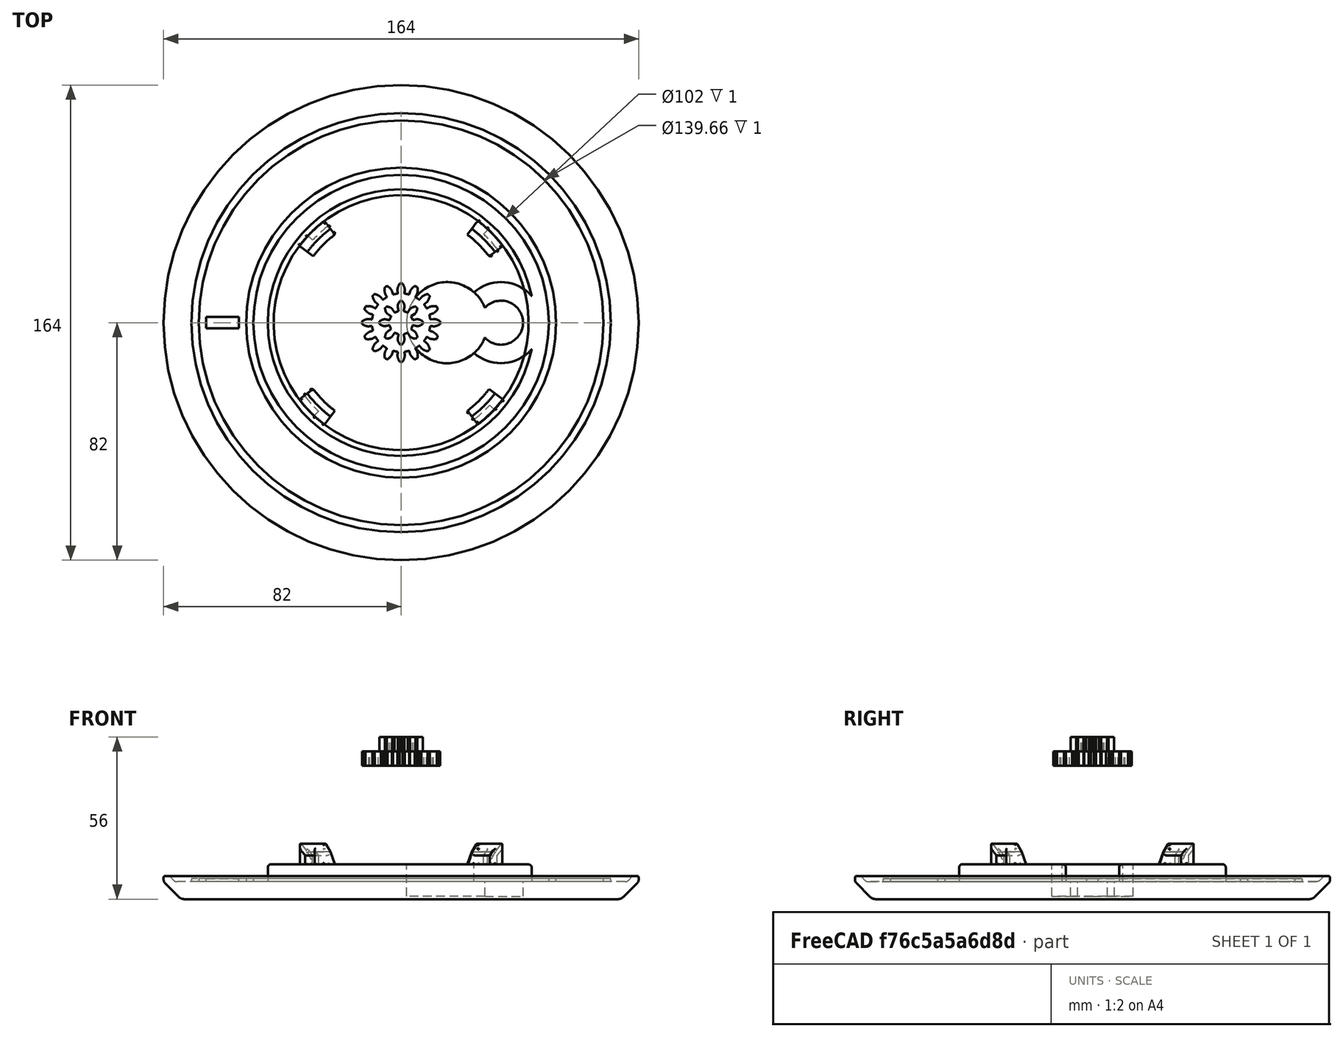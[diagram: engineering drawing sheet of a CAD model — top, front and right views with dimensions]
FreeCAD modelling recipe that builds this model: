
FCSTD DOCUMENT  (FreeCAD 1.0R39319 (Git))
Label: smart_medication_box_v2
License: All rights reserved
LicenseURL: https://en.wikipedia.org/wiki/All_rights_reserved
objects: Sketcher::SketchObject×25, PartDesign::Fillet×14, PartDesign::Body×11, PartDesign::Pad×8, PartDesign::Revolution×8, App::FeaturePython×7, PartDesign::Pocket×6, App::Link×6, PartDesign::PolarPattern×5, Part::FeaturePython×4, PartDesign::FeaturePython×3, TechDraw::DrawSVGTemplate×3, TechDraw::DrawProjGroupItem×3, TechDraw::DrawPage×3, PartDesign::Chamfer×2, TechDraw::DrawViewDimension×2, App::VarSet×1, PartDesign::AdditivePipe×1, Part::Cut×1, PartDesign::FeatureBase×1, +4 more types
note: 206 computed .brp shape members not serialized (recipe doc carries the construction recipe); baked Part::Feature solids carry a one-line shape summary decoded from their .brp

FEATURE [Part::FeaturePython] BevelGear  # WARN: FeaturePython — macro-defined, semantics opaque (R4)
  AttacherType = Attacher::AttachEngine3D
  angular_backlash = 0
  backlash = 0
  beta = 0
  clearance = 0.1
  dw = 32
  height = 7.5
  module = 2
  num_teeth = 16
  numpoints = 20
  pitch_angle = 45
  pressure_angle = 20
  reset_origin = true
  version = 1.3.0
  expr: angular_backlash = backlash / dw * 360 ° / pi
  expr: dw = num_teeth * module
  expr: height = 7.5
  expr: module = 2
  expr: num_teeth = 16
FEATURE [Sketcher::SketchObject] Sketch
  ArcFitTolerance = 1e-06
  AttachmentSupport = -> [Origin002]
  FullyConstrained = true
  MakeInternals = false
  MapMode = 5
  expr: Constraints[1] = 2 * VarSet.outer_ring_center_radius
  sketch-geometry (1):
    g0: Circle CenterX=0 CenterY=0 CenterZ=0 NormalX=0 NormalY=0 NormalZ=1 AngleXU=0 Radius=100
  constraints (2):
    c: Coincident(g0,g-1)
    c: Diameter(g0) = 200
FEATURE [App::VarSet] VarSet
  fillet_oouter_gear = 0.8
  outer_gear_section_length = 48
  outer_ring_bottom_width = 50
  outer_ring_center_radius = 100
  outer_ring_height = 36
  outer_ring_sides_angle = 30
  outer_wall_thickness = 2
  wall_thickness = 2
  expr: fillet_oouter_gear = 0.8
  expr: outer_ring_bottom_width = 50
  expr: outer_ring_center_radius = 100
  expr: outer_ring_height = 36
  expr: outer_ring_sides_angle = 30
FEATURE [Sketcher::SketchObject] Sketch002
  ArcFitTolerance = 1e-06
  FullyConstrained = true
  MakeInternals = false
  MapMode = 5
  Placement = pos=(100,0,0) rot=(1,0,0;1.5708rad)
  expr: Constraints[13] = VarSet.outer_ring_height
  expr: Constraints[16] = VarSet.outer_ring_sides_angle
  expr: Constraints[17] = VarSet.outer_ring_sides_angle
  expr: Constraints[19] = 5
  expr: Constraints[21] = VarSet.wall_thickness * 2
  expr: Constraints[24] = VarSet.wall_thickness
  expr: Constraints[28] = VarSet.outer_ring_bottom_width
  expr: Constraints[7] = VarSet.wall_thickness
  expr: Constraints[8] = VarSet.outer_ring_height
  expr: Constraints[9] = VarSet.wall_thickness
  sketch-geometry (10):
    g0: LineSegment StartX=26.1547 StartY=0 StartZ=0 EndX=46.9393 EndY=36 EndZ=0
    g1: LineSegment StartX=46.9393 StartY=36 StartZ=0 EndX=44.6299 EndY=36 EndZ=0
    g2: LineSegment StartX=44.6299 StartY=36 StartZ=0 EndX=25 EndY=2 EndZ=0
    g3: LineSegment StartX=25 StartY=2 StartZ=0 EndX=-25 EndY=2 EndZ=0
    g4: LineSegment StartX=-25 StartY=2 StartZ=0 EndX=-44.6299 EndY=36 EndZ=0
    g5: LineSegment StartX=-44.6299 StartY=36 StartZ=0 EndX=-49.2487 EndY=36 EndZ=0
    g6: LineSegment StartX=-26.1547 StartY=0 StartZ=0 EndX=26.1547 EndY=0 EndZ=0
    g7: LineSegment StartX=-49.2487 StartY=36 StartZ=0 EndX=-46.362 EndY=31 EndZ=0
    g8: LineSegment StartX=-44.0526 StartY=31 StartZ=0 EndX=-26.1547 EndY=0 EndZ=0
    g9: LineSegment StartX=-44.0526 StartY=31 StartZ=0 EndX=-46.362 EndY=31 EndZ=0
  constraints (29):
    c: Coincident(g1,g0)
    c: Coincident(g1,g2)
    c: Coincident(g2,g3)
    c: Coincident(g3,g4)
    c: Coincident(g4,g5)
    c: Horizontal(g5)
    c: Coincident(g6,g0)
    c: Distance(g0,g2) = 2
    c: DistanceY(g6,g4) = 36
    c: DistanceY(g6,g3) = 2
    c: Parallel(g3,g6)
    c: Parallel(g1,g-1)
    c: Parallel(g0,g2)
    c: Distance(g-1,g1) = 36
    c: Symmetric(g6,g0,g-2)
    c: PointOnObject(g0,g-1)
    c: Angle(g2,g-2) = 0.523599
    c: Angle(g-2,g4) = 0.523599
    c: Coincident(g7,g5)
    c: DistanceY(g7,g5) = 5
    c: Parallel(g7,g4)
    c: Distance(g4,g7) = 4
    c: Coincident(g8,g6)
    c: Parallel(g8,g4)
    c: Distance(g4,g8) = 2
    c: Coincident(g9,g8)
    c: Coincident(g9,g7)
    c: Parallel(g9,g5)
    c: DistanceX(g3,g3) = 50
FEATURE [PartDesign::AdditivePipe] AdditivePipe
  AuxilleryCurvelinear = true
  AuxillerySpineTangent = false
  Binormal = (0,0,0)
  Mode = 0
  Placement = pos=(100,0,0) rot=(1,0,0;1.5708rad)
  Profile = -> Sketch002
  Refine = true
  Spine = -> Sketch
  SpineTangent = false
  Suppressed = false
  Transformation = 0
  Transition = 0
FEATURE [PartDesign::Body] Body001  label="outer_sections_ring_gear"
  AllowCompound = false
  Group = -> [Sketch,Sketch002,AdditivePipe]
  Origin = -> Origin002
  Tip = -> AdditivePipe
FEATURE [PartDesign::FeaturePython] BevelGear001  # WARN: FeaturePython — macro-defined, semantics opaque (R4)
  AttacherType = Attacher::AttachEngine3D
  Suppressed = false
  angular_backlash = 0
  backlash = 0
  beta = 0
  clearance = 0.1
  dw = 96
  height = 5
  module = 1.5
  num_teeth = 64
  numpoints = 20
  pitch_angle = 30
  pressure_angle = 20
  reset_origin = true
  version = 1.3.0
  expr: angular_backlash = backlash / dw * 360 ° / pi
  expr: dw = num_teeth * module
  expr: module = 1.5
  expr: num_teeth = 64
  expr: pitch_angle = 30
FEATURE [PartDesign::Body] Body002  label="Body"
  AllowCompound = false
  Group = -> [BevelGear001]
  Origin = -> Origin004
  Placement = pos=(0,0,45) rot=(0,0,1;0rad)
  Tip = -> BevelGear001
FEATURE [Part::Cut] Cut
  Base = -> Body001
  Refine = true
  Tool = -> Body002
FEATURE [Sketcher::SketchObject] Sketch003
  ArcFitTolerance = 1e-06
  AttachmentSupport = -> [Origin006,XY_Plane003]
  FullyConstrained = true
  MakeInternals = true
  MapMode = 5
  expr: Constraints[0] = 104
  sketch-geometry (1):
    g0: Circle CenterX=0 CenterY=0 CenterZ=0 NormalX=0 NormalY=0 NormalZ=1 AngleXU=0 Radius=52
  constraints (2):
    c: Diameter(g0) = 104
    c: Coincident(g0,g-1)
FEATURE [PartDesign::Pad] Pad
  Direction = (0,0,1)
  Length = 6
  Length2 = 10
  Profile = -> Sketch003
  ReferenceAxis = -> Sketch003 [N_Axis]
  Refine = true
  Suppressed = false
  Type = 0
  expr: Length = 6
FEATURE [Sketcher::SketchObject] Sketch004
  ArcFitTolerance = 1e-06
  AttachmentSupport = -> [Pad]
  FullyConstrained = true
  MakeInternals = false
  MapMode = 5
  Placement = pos=(0,0,6) rot=(0,0,1;0rad)
  expr: Constraints[0] = 48 * 2 - 2
  sketch-geometry (1):
    g0: Circle CenterX=0 CenterY=0 CenterZ=0 NormalX=0 NormalY=0 NormalZ=1 AngleXU=0 Radius=47
  constraints (2):
    c: Diameter(g0) = 94
    c: Coincident(g0,g-1)
FEATURE [PartDesign::Pad] Pad001
  BaseFeature = -> Pad
  Direction = (0,0,1)
  Length = 6
  Length2 = 10
  Profile = -> Sketch004
  ReferenceAxis = -> Sketch004 [N_Axis]
  Refine = true
  Suppressed = false
  Type = 0
  expr: Length = 6
FEATURE [Part::FeaturePython] InvoluteGear  # WARN: FeaturePython — macro-defined, semantics opaque (R4)
  AttacherType = Attacher::AttachEngine3D
  Placement = pos=(0,0,41) rot=(0,0,1;0rad)
  addendum_diameter = 15
  angular_backlash = 0
  axle_hole = false
  axle_holesize = 10
  backlash = 0
  clearance = 0.25
  double_helix = false
  head = 0
  head_fillet = 0
  height = 5
  helix_angle = 0
  module = 1.5
  num_teeth = 8
  numpoints = 20
  offset_hole = false
  offset_holeoffset = 10
  offset_holesize = 10
  pitch_diameter = 12
  pressure_angle = 20
  properties_from_tool = false
  reversed_backlash = false
  root_diameter = 8.25
  root_fillet = 0
  shift = 0
  simple = false
  transverse_pitch = 4.71239
  traverse_module = 1.5
  undercut = false
  version = 1.3.0
  expr: angular_backlash = backlash / pitch_diameter * 360 ° / pi
  expr: module = 1.5
  expr: num_teeth = 8
FEATURE [Sketcher::SketchObject] Sketch005
  ArcFitTolerance = 1e-06
  AttachmentSupport = -> [Pad001]
  ExternalGeometry = -> [Pad001]
  FullyConstrained = true
  MakeInternals = false
  MapMode = 5
  Placement = pos=(0,0,12) rot=(0,0,1;0rad)
  expr: Constraints[0] = 28
  expr: Constraints[4] = 11.5
  sketch-geometry (2):
    g0: Circle CenterX=35.5 CenterY=0 CenterZ=0 NormalX=0 NormalY=0 NormalZ=1 AngleXU=0 Radius=14
    g1: Circle [constr] CenterX=35.5 CenterY=0 CenterZ=0 NormalX=0 NormalY=0 NormalZ=1 AngleXU=0 Radius=11.5
  constraints (5):
    c: Diameter(g0) = 28
    c: Coincident(g1,g0)
    c: Tangent(g1,g-3)
    c: PointOnObject(g0,g-1)
    c: Distance(g0,g-3) = 11.5
FEATURE [PartDesign::Pocket] Pocket001
  BaseFeature = -> Pad001
  Direction = (0,0,-1)
  Length = 6
  Length2 = 5
  Profile = -> Sketch005
  ReferenceAxis = -> Sketch005 [N_Axis]
  Refine = true
  Suppressed = false
  Type = 0
  expr: Length = 6
FEATURE [Sketcher::SketchObject] Sketch006
  ArcFitTolerance = 1e-06
  AttachmentSupport = -> [Pocket001]
  ExternalGeometry = -> [Pocket001]
  FullyConstrained = true
  MakeInternals = false
  MapMode = 5
  Placement = pos=(0,0,6) rot=(0,0,1;0rad)
  sketch-geometry (1):
    g0: Circle CenterX=35.5 CenterY=0 CenterZ=0 NormalX=0 NormalY=0 NormalZ=1 AngleXU=0 Radius=7.6
  constraints (2):
    c: Diameter(g0) = 15.2
    c: Coincident(g0,g-4)
FEATURE [PartDesign::Pocket] Pocket002
  BaseFeature = -> Pocket001
  Direction = (0,0,-1)
  Length = 5
  Length2 = 5
  Profile = -> Sketch006
  ReferenceAxis = -> Sketch006 [N_Axis]
  Refine = true
  Suppressed = false
  Type = 0
FEATURE [PartDesign::FeaturePython] InvoluteGear001  # WARN: FeaturePython — macro-defined, semantics opaque (R4)
  AttacherType = Attacher::AttachEngine3D
  Suppressed = false
  addendum_diameter = 27
  angular_backlash = 0
  axle_hole = false
  axle_holesize = 10
  backlash = 0
  clearance = 0.25
  double_helix = false
  head = 0
  head_fillet = 0
  height = 5
  helix_angle = 0
  module = 1.5
  num_teeth = 16
  numpoints = 20
  offset_hole = false
  offset_holeoffset = 10
  offset_holesize = 10
  pitch_diameter = 24
  pressure_angle = 20
  properties_from_tool = false
  reversed_backlash = false
  root_diameter = 20.25
  root_fillet = 0
  shift = 0
  simple = false
  transverse_pitch = 4.71239
  traverse_module = 1.5
  undercut = false
  version = 1.3.0
  expr: angular_backlash = backlash / pitch_diameter * 360 ° / pi
  expr: module = 1.5
  expr: num_teeth = 16
FEATURE [Sketcher::SketchObject] Sketch007
  ArcFitTolerance = 1e-06
  AttachmentSupport = -> [Pocket002]
  ExternalGeometry = -> [Pocket002]
  FullyConstrained = true
  MakeInternals = false
  MapMode = 5
  Placement = pos=(0,0,12) rot=(0,0,1;0rad)
  expr: Constraints[0] = 28
  expr: Constraints[2] = -3
  sketch-geometry (1):
    g0: Circle CenterX=16.9 CenterY=0 CenterZ=0 NormalX=0 NormalY=0 NormalZ=1 AngleXU=0 Radius=14
  constraints (3):
    c: Diameter(g0) = 28
    c: PointOnObject(g0,g-1)
    c: Distance(g0,g-3) = -3
FEATURE [PartDesign::Pocket] Pocket003
  BaseFeature = -> Pocket002
  Direction = (0,0,-1)
  Length = 11
  Length2 = 5
  Profile = -> Sketch007
  ReferenceAxis = -> Sketch007 [N_Axis]
  Refine = true
  Suppressed = false
  Type = 0
  expr: Length = 11
FEATURE [Sketcher::SketchObject] Sketch008
  ArcFitTolerance = 1e-06
  AttachmentSupport = -> [InvoluteGear001]
  FullyConstrained = true
  MakeInternals = false
  MapMode = 5
  Placement = pos=(0,0,5) rot=(0,0,1;0rad)
  expr: Constraints[11] = 3.1
  sketch-geometry (4):
    g0: ArcOfCircle CenterX=0 CenterY=0 CenterZ=0 NormalX=0 NormalY=0 NormalZ=1 AngleXU=0 Radius=2.5 StartAngle=2.47285 EndAngle=3.81034
    g1: ArcOfCircle CenterX=0 CenterY=0 CenterZ=0 NormalX=0 NormalY=0 NormalZ=1 AngleXU=0 Radius=2.5 StartAngle=5.61444 EndAngle=6.95193
    g2: LineSegment StartX=-1.9615 StartY=1.55 StartZ=0 EndX=1.9615 EndY=1.55 EndZ=0
    g3: LineSegment StartX=1.9615 StartY=-1.55 StartZ=0 EndX=-1.9615 EndY=-1.55 EndZ=0
  constraints (12):
    c: Coincident(g0,g-1)
    c: Coincident(g0,g1)
    c: Diameter(g0) = 5
    c: Equal(g1,g0)
    c: Coincident(g2,g0)
    c: Coincident(g2,g1)
    c: Coincident(g3,g1)
    c: Coincident(g3,g0)
    c: Parallel(g3,g2)
    c: Parallel(g-1,g2)
    c: Equal(g2,g3)
    c: Distance(g3,g2) = 3.1
FEATURE [PartDesign::Pocket] Pocket004
  BaseFeature = -> InvoluteGear001
  Direction = (0,0,-1)
  Length = 5
  Length2 = 5
  Profile = -> Sketch008
  ReferenceAxis = -> Sketch008 [N_Axis]
  Refine = true
  Suppressed = false
  Type = 0
FEATURE [App::Link] Body006  label="base"
  LinkedObject = -> Body003
FEATURE [Part::FeaturePython] InvoluteGear002  # WARN: FeaturePython — macro-defined, semantics opaque (R4)
  AttacherType = Attacher::AttachEngine3D
  Placement = pos=(0,0,46) rot=(0,0,1;0rad)
  addendum_diameter = 27
  angular_backlash = 0
  axle_hole = false
  axle_holesize = 10
  backlash = 0
  clearance = 0.25
  double_helix = false
  head = 0
  head_fillet = 0
  height = 5
  helix_angle = 0
  module = 1.5
  num_teeth = 16
  numpoints = 20
  offset_hole = false
  offset_holeoffset = 10
  offset_holesize = 10
  pitch_diameter = 24
  pressure_angle = 20
  properties_from_tool = false
  reversed_backlash = false
  root_diameter = 20.25
  root_fillet = 0
  shift = 0
  simple = false
  transverse_pitch = 4.71239
  traverse_module = 1.5
  undercut = false
  version = 1.3.0
  expr: angular_backlash = backlash / pitch_diameter * 360 ° / pi
  expr: module = 1.5
FEATURE [PartDesign::FeaturePython] InternalInvoluteGear  # WARN: FeaturePython — macro-defined, semantics opaque (R4)
  AttacherType = Attacher::AttachEngine3D
  Suppressed = false
  addendum_diameter = 94.2
  angular_backlash = 0
  backlash = 0
  clearance = 0.2
  double_helix = false
  head = -0.4
  head_fillet = 0
  height = 5
  helix_angle = 0
  module = 1.5
  num_teeth = 64
  numpoints = 20
  outside_diameter = 106
  pitch_diameter = 96
  pressure_angle = 20
  properties_from_tool = false
  reversed_backlash = false
  root_diameter = 99.6
  root_fillet = 0
  shift = 0
  simple = false
  thickness = 5
  transverse_pitch = 4.71239
  version = 1.3.0
  expr: angular_backlash = backlash / pitch_diameter * 360 ° / pi
  expr: clearance = 0.2
  expr: module = 1.5
  expr: num_teeth = 64
  expr: pressure_angle = 20
FEATURE [PartDesign::FeatureBase] BaseFeature002
  BaseFeature = -> InvoluteGear002
  Suppressed = false
FEATURE [PartDesign::Body] Body017
  AllowCompound = false
  BaseFeature = -> InvoluteGear002
  Group = -> [BaseFeature002]
  Origin = -> Origin028
  Placement = pos=(0,0,46) rot=(0,0,1;0rad)
  Tip = -> BaseFeature002
FEATURE [Part::FeaturePython] InvoluteGear003  # WARN: FeaturePython — macro-defined, semantics opaque (R4)
  AttacherType = Attacher::AttachEngine3D
  Placement = pos=(0,0,51) rot=(0,0,1;0rad)
  addendum_diameter = 15
  angular_backlash = 0
  axle_hole = false
  axle_holesize = 10
  backlash = 0
  clearance = 0.25
  double_helix = false
  head = 0
  head_fillet = 0
  height = 5
  helix_angle = 0
  module = 1.5
  num_teeth = 8
  numpoints = 20
  offset_hole = false
  offset_holeoffset = 10
  offset_holesize = 10
  pitch_diameter = 12
  pressure_angle = 20
  properties_from_tool = false
  reversed_backlash = false
  root_diameter = 8.25
  root_fillet = 0
  shift = 0
  simple = false
  transverse_pitch = 4.71239
  traverse_module = 1.5
  undercut = false
  version = 1.3.0
  expr: angular_backlash = backlash / pitch_diameter * 360 ° / pi
  expr: module = 1.5
  expr: num_teeth = 8
FEATURE [PartDesign::Boolean] Boolean
  Group = -> [InvoluteGear003,InvoluteGear002,Body017]
  Refine = true
  Suppressed = false
  Type = 0
  UsePlacement = true
FEATURE [App::Link] Body019  label="middle_gear"
  LinkPlacement = pos=(34.5001,-1.27229e-05,57) rot=(-0.64511,0.76409,0;3.14159rad)
  LinkedObject = -> Body018
  Placement = pos=(34.5001,-1.27229e-05,57) rot=(-0.64511,0.76409,0;3.14159rad)
FEATURE [App::Link] motor_gear001  label="motor_gear"
  LinkPlacement = pos=(15.9,0,1) rot=(0,0,-1;2.47285rad)
  LinkedObject = -> Body005
  Placement = pos=(15.9,0,1) rot=(0,0,-1;2.47285rad)
FEATURE [App::Link] outer_gear  label="pill_sections"
  LinkPlacement = pos=(7e-16,7e-16,6) rot=(0,0,1;0rad)
  LinkedObject = -> Body016
  Placement = pos=(7e-16,7e-16,6) rot=(0,0,1;0rad)
FEATURE [Sketcher::SketchObject] Sketch009
  ArcFitTolerance = 1e-06
  FullyConstrained = true
  MakeInternals = false
  MapMode = 5
  Placement = pos=(53,0,0) rot=(1,0,0;1.5708rad)
  expr: Constraints[10] = 2
  expr: Constraints[3] = 22
  sketch-geometry (17):
    g0: LineSegment StartX=0 StartY=0 StartZ=0 EndX=0 EndY=3 EndZ=0
    g1: LineSegment StartX=0 StartY=3 StartZ=0 EndX=21.1716 EndY=3 EndZ=0
    g2: LineSegment StartX=22.5858 StartY=3.58579 StartZ=0 EndX=23.7071 EndY=4.70711 EndZ=0
    g3: LineSegment StartX=24.4142 StartY=5 StartZ=0 EndX=25.4142 EndY=5 EndZ=0
    g4: LineSegment StartX=26.4142 StartY=4 StartZ=0 EndX=26.4142 EndY=3.82843 EndZ=0
    g5: LineSegment StartX=25.8284 StartY=2.41421 StartZ=0 EndX=24 EndY=0.585786 EndZ=0
    g6: LineSegment StartX=0 StartY=0 StartZ=0 EndX=22.5858 EndY=0 EndZ=0
    g7: ArcOfCircle CenterX=25.4142 CenterY=4 CenterZ=0 NormalX=0 NormalY=0 NormalZ=1 AngleXU=0 Radius=1 StartAngle=0 EndAngle=1.5708
    g8: GeomPoint [constr] X=26.4142 Y=5 Z=0
    g9: ArcOfCircle CenterX=24.4142 CenterY=4 CenterZ=0 NormalX=0 NormalY=0 NormalZ=1 AngleXU=0 Radius=1 StartAngle=1.5708 EndAngle=2.35619
    g10: GeomPoint [constr] X=24 Y=5 Z=0
    g11: ArcOfCircle CenterX=24.4142 CenterY=3.82843 CenterZ=0 NormalX=0 NormalY=0 NormalZ=1 AngleXU=0 Radius=2 StartAngle=5.49779 EndAngle=6.28319
    g12: GeomPoint [constr] X=26.4142 Y=3 Z=0
    g13: ArcOfCircle CenterX=21.1716 CenterY=5 CenterZ=0 NormalX=0 NormalY=0 NormalZ=1 AngleXU=0 Radius=2 StartAngle=4.71239 EndAngle=5.49779
    g14: GeomPoint [constr] X=22 Y=3 Z=0
    g15: ArcOfCircle CenterX=22.5858 CenterY=2 CenterZ=0 NormalX=0 NormalY=0 NormalZ=1 AngleXU=0 Radius=2 StartAngle=4.71239 EndAngle=5.49779
    g16: GeomPoint [constr] X=23.4142 Y=0 Z=0
  constraints (40):
    c: Coincident(g-1,g0)
    c: Coincident(g0,g1)
    c: PointOnObject(g0,g-2)
    c: DistanceX(g1,g14) = 22
    c: PointOnObject(g16,g-1)
    c: Coincident(g6,g0)
    c: Parallel(g1,g6)
    c: Parallel(g3,g1)
    c: Perpendicular(g3,g4)
    c: PointOnObject(g12,g1)
    c: DistanceY(g12,g8) = 2
    c: PointOnObject(g8,g3)
    c: PointOnObject(g8,g4)
    c: Tangent(g3,g7) = 1.5708
    c: Tangent(g4,g7) = 1.5708
    c: PointOnObject(g10,g2)
    c: PointOnObject(g10,g3)
    c: Tangent(g2,g9) = 1.5708
    c: Tangent(g3,g9) = 1.5708
    c: PointOnObject(g12,g5)
    c: PointOnObject(g12,g4)
    c: Tangent(g5,g11) = 1.5708
    c: Tangent(g4,g11) = 1.5708
    c: PointOnObject(g14,g2)
    c: PointOnObject(g14,g1)
    c: Tangent(g2,g13) = -1.5708
    c: Tangent(g1,g13) = -1.5708
    c: PointOnObject(g16,g5)
    c: PointOnObject(g16,g6)
    c: Tangent(g5,g15) = 1.5708
    c: Tangent(g6,g15) = -1.5708
    c: Equal(g9,g7)
    c: Equal(g13,g11)
    c: Equal(g11,g15)
    c: Radius(g9) = 1
    c: Radius(g13) = 2
    c: Parallel(g5,g2)
    c: Angle(g-1,g5) = 0.785398
    c: DistanceY(g0,g0) = 3
    c: Distance(g3,g3) = 1
FEATURE [PartDesign::Revolution] Revolution
  Angle = 360
  Angle2 = 60
  Axis = (1e-16,1e-16,1)
  Base = (0,0,0)
  BaseFeature = -> Pocket003
  Profile = -> Sketch009
  ReferenceAxis = -> Z_Axis003
  Refine = true
  Reversed = true
  Suppressed = false
  Type = 0
FEATURE [Sketcher::SketchObject] Sketch010
  ArcFitTolerance = 1e-06
  ExternalGeometry = -> [InternalInvoluteGear]
  FullyConstrained = false
  MakeInternals = false
  MapMode = 5
  Placement = pos=(53,0,0) rot=(1,0,0;1.5708rad)
  expr: Constraints[10] = VarSet.outer_wall_thickness
  expr: Constraints[11] = VarSet.outer_wall_thickness
  expr: Constraints[14] = VarSet.outer_wall_thickness
  expr: Constraints[17] = VarSet.fillet_oouter_gear
  expr: Constraints[2] = 5
  expr: Constraints[34] = VarSet.outer_wall_thickness
  expr: Constraints[36] = VarSet.outer_ring_height
  expr: Constraints[37] = VarSet.fillet_oouter_gear
  expr: Constraints[38] = 30
  expr: Constraints[45] = VarSet.fillet_oouter_gear
  expr: Constraints[50] = 25
  expr: Constraints[52] = 10
  expr: Constraints[6] = 25
  expr: Constraints[9] = VarSet.outer_wall_thickness
  sketch-geometry (28):
    g0: LineSegment StartX=0 StartY=0 StartZ=0 EndX=0 EndY=5 EndZ=0
    g1: LineSegment StartX=0 StartY=0 StartZ=0 EndX=24.0192 EndY=0 EndZ=0
    g2: LineSegment StartX=25.6005 StartY=0.775418 StartZ=0 EndX=40.7862 EndY=20.3842 EndZ=0
    g3: LineSegment StartX=24.6198 StartY=2.77542 StartZ=0 EndX=39.2049 EndY=21.6088 EndZ=0
    g4: LineSegment StartX=9.57963 StartY=2 StartZ=0 EndX=23.0385 EndY=2 EndZ=0
    g5: LineSegment StartX=0 StartY=5 StartZ=0 EndX=-2 EndY=5 EndZ=0
    g6: LineSegment StartX=-0.122418 StartY=35.2036 StartZ=0 EndX=4.22e-14 EndY=7.67973 EndZ=0
    g7: LineSegment StartX=8.57963 StartY=2.26795 StartZ=0 EndX=0.399992 EndY=6.99046 EndZ=0
    g8: ArcOfCircle CenterX=0.799992 CenterY=7.68328 CenterZ=0 NormalX=0 NormalY=0 NormalZ=1 AngleXU=0 Radius=0.8 StartAngle=3.14604 EndAngle=4.18879
    g9: ArcOfCircle CenterX=9.57963 CenterY=4 CenterZ=0 NormalX=0 NormalY=0 NormalZ=1 AngleXU=0 Radius=2 StartAngle=4.18879 EndAngle=4.71239
    g10: GeomPoint [constr] X=9.04373 Y=2 Z=0
    g11: ArcOfCircle CenterX=23.0385 CenterY=4 CenterZ=0 NormalX=0 NormalY=0 NormalZ=1 AngleXU=0 Radius=2 StartAngle=4.71239 EndAngle=5.62423
    g12: GeomPoint [constr] X=24.0192 Y=2 Z=0
    g13: ArcOfCircle CenterX=24.0192 CenterY=2 CenterZ=0 NormalX=0 NormalY=0 NormalZ=1 AngleXU=0 Radius=2 StartAngle=4.71239 EndAngle=5.62423
    g14: GeomPoint [constr] X=25 Y=0 Z=0
    g15: GeomPoint [constr] X=29 Y=5.16508 Z=0
    g16: GeomPoint [constr] X=27 Y=5.84896 Z=0
    g17: ArcOfCircle CenterX=-0.92241 CenterY=35.2 CenterZ=0 NormalX=0 NormalY=0 NormalZ=1 AngleXU=0 Radius=0.8 StartAngle=0.00444768 EndAngle=1.5708
    g18: LineSegment StartX=-10.9224 StartY=36 StartZ=0 EndX=-5.92241 EndY=36 EndZ=0
    g19: ArcOfCircle CenterX=19.4391 CenterY=36.916 CenterZ=0 NormalX=0 NormalY=0 NormalZ=1 AngleXU=0 Radius=27 StartAngle=5.62423 EndAngle=6.21764
    g20: ArcOfCircle CenterX=19.4391 CenterY=36.916 CenterZ=0 NormalX=0 NormalY=0 NormalZ=1 AngleXU=0 Radius=25 StartAngle=5.62423 EndAngle=6.21662
    g21: ArcOfCircle CenterX=45.1819 CenterY=35.2 CenterZ=0 NormalX=0 NormalY=0 NormalZ=1 AngleXU=0 Radius=0.8 StartAngle=1.5708 EndAngle=3.07503
    g22: LineSegment StartX=45.5828 StartY=36 StartZ=0 EndX=45.1819 EndY=36 EndZ=0
    g23: ArcOfCircle CenterX=45.5828 CenterY=35.2 CenterZ=0 NormalX=0 NormalY=0 NormalZ=1 AngleXU=0 Radius=0.8 StartAngle=6.21764 EndAngle=7.85398
    g24: ArcOfCircle CenterX=-10.9224 CenterY=35.2 CenterZ=0 NormalX=0 NormalY=0 NormalZ=1 AngleXU=0 Radius=0.8 StartAngle=1.5708 EndAngle=3.66964
    g25: LineSegment StartX=-11.6134 StartY=34.7969 StartZ=0 EndX=-2.05968 EndY=18.418 EndZ=0
    g26: LineSegment StartX=-2.05968 StartY=18.418 StartZ=0 EndX=-2 EndY=5 EndZ=0
    g27: LineSegment StartX=-5.92241 StartY=36 StartZ=0 EndX=-0.92241 EndY=36 EndZ=0
  constraints (66):
    c: Coincident(g0,g-1)
    c: PointOnObject(g0,g-2)
    c: DistanceY(g0,g0) = 5
    c: Coincident(g1,g0)
    c: PointOnObject(g14,g-1)
    c: Parallel(g3,g2)
    c: DistanceX(g1,g14) = 25
    c: DistanceX(g14,g15) = 4
    c: Parallel(g4,g1)
    c: Distance(g1,g4) = 2
    c: DistanceX(g16,g15) = 2
    c: Distance(g14,g3) = 2
    c: Coincident(g5,g0)
    c: Horizontal(g5)
    c: DistanceX(g5,g5) = 2
    c: Tangent(g8,g7) = 1.5708
    c: Tangent(g8,g6) = -1.5708
    c: Radius(g8) = 0.8
    c: PointOnObject(g6,g-2)
    c: PointOnObject(g10,g7)
    c: PointOnObject(g10,g4)
    c: Tangent(g7,g9) = 1.5708
    c: Tangent(g4,g9) = -1.5708
    c: PointOnObject(g12,g4)
    c: PointOnObject(g12,g3)
    c: Tangent(g4,g11) = -1.5708
    c: Tangent(g3,g11) = -1.5708
    c: PointOnObject(g14,g1)
    c: PointOnObject(g14,g2)
    c: Tangent(g1,g13) = -1.5708
    c: Tangent(g2,g13) = -1.5708
    c: PointOnObject(g15,g2)
    c: PointOnObject(g16,g3)
    c: Equal(g13,g11)
    c: Distance(g0,g8) = 2
    c: Tangent(g17,g6) = 1.5708
    c: Distance(g18,g-1) = 36
    c: Radius(g17) = 0.8
    c: Angle(g7,g1) = 0.523599
    c: Equal(g11,g9)
    c: Coincident(g20,g19)
    c: Tangent(g20,g3) = -1.5708
    c: Tangent(g19,g2) = -1.5708
    c: Tangent(g22,g21) = -1.5708
    c: Tangent(g21,g20) = 1.5708
    c: Radius(g21) = 0.8
    c: Tangent(g23,g22) = -1.5708
    c: Tangent(g23,g19) = -1.5708
    c: Equal(g23,g21)
    c: Parallel(g22,g-1)
    c: Radius(g20) = 25
    c: Radius(g11) = 2
    c: DistanceX(g18,g27) = 10
    c: Tangent(g24,g18) = 1.5708
    c: Equal(g24,g17)
    c: Coincident(g26,g25)
    c: Coincident(g26,g5)
    c: Parallel(g26,g6)
    c: Tangent(g25,g24) = -1.5708
    c: Perpendicular(g-2,g18)
    c: Perpendicular(g-2,g27)
    c: Coincident(g18,g27)
    c: Tangent(g27,g17) = 1.5708
    c: Equal(g27,g18)
    c: Angle(g26,g25) = 0.523599
    c: Vertical(g18,g-3)
FEATURE [PartDesign::Revolution] Revolution001
  Angle = 360
  Angle2 = 60
  Axis = (1e-16,1e-16,1)
  Base = (0,0,0)
  BaseFeature = -> InternalInvoluteGear
  Profile = -> Sketch010
  ReferenceAxis = -> Z_Axis013
  Refine = true
  Reversed = true
  Suppressed = false
  Type = 0
FEATURE [Sketcher::SketchObject] Sketch011
  ArcFitTolerance = 1e-06
  ExternalGeometry = -> [Revolution001]
  FullyConstrained = true
  MakeInternals = false
  MapMode = 5
  Placement = pos=(53,0,0) rot=(1,0,0;1.5708rad)
  sketch-geometry (2):
    g0: LineSegment StartX=-0.92241 StartY=36 StartZ=0 EndX=45.1819 EndY=36 EndZ=0
    g1: LineSegment StartX=9.57963 StartY=2 StartZ=0 EndX=23.0385 EndY=2 EndZ=0
  constraints (4):
    c: Coincident(g0,g-11)
    c: Coincident(g0,g-7)
    c: Tangent(g1,g-6) = -1.5708
    c: Coincident(g1,g-8)
FEATURE [PartDesign::Revolution] Revolution002
  Angle = 1
  Angle2 = 60
  Axis = (1e-16,1e-16,1)
  Base = (0,0,0)
  BaseFeature = -> Revolution001
  Midplane = true
  Profile = -> Sketch011
  ReferenceAxis = -> Z_Axis013
  Refine = true
  Suppressed = false
  Type = 0
  expr: Angle = 1
FEATURE [PartDesign::PolarPattern] PolarPattern
  Angle = 360
  Axis = -> Z_Axis013
  BaseFeature = -> Revolution002
  Mode = 0
  Occurrences = 32
  Offset = 120
  Originals = -> [Revolution002]
  Refine = true
  Suppressed = false
  TransformMode = 0
  expr: Occurrences = 32
FEATURE [PartDesign::Fillet] Fillet
  Base = -> Revolution [Edge30]
  BaseFeature = -> Revolution
  Radius = 1
  Refine = true
  SupportTransform = false
  Suppressed = false
  UseAllEdges = false
FEATURE [PartDesign::Fillet] Fillet001
  Base = -> Boolean [Face4]
  BaseFeature = -> Boolean
  Radius = 0.25
  Refine = true
  SupportTransform = false
  Suppressed = false
  UseAllEdges = false
  expr: Radius = 0.25
FEATURE [PartDesign::Fillet] Fillet002
  Base = -> Fillet001 [Face4,Face243]
  BaseFeature = -> Fillet001
  Radius = 0.2
  Refine = true
  SupportTransform = false
  Suppressed = false
  UseAllEdges = false
  expr: Radius = 0.2
FEATURE [PartDesign::Body] Body018
  AllowCompound = false
  Group = -> [Boolean,Fillet001,Fillet002]
  Origin = -> Origin030
  Tip = -> Fillet002
FEATURE [PartDesign::Body] Body020  label="upper_cover"
  AllowCompound = false
  Origin = -> Origin032
FEATURE [Sketcher::SketchObject] Sketch012
  ArcFitTolerance = 1e-06
  AttachmentSupport = -> [Origin034]
  FullyConstrained = true
  MakeInternals = false
  MapMode = 5
  expr: Constraints[2] = 80
  sketch-geometry (3):
    g0: Circle CenterX=0 CenterY=0 CenterZ=0 NormalX=0 NormalY=0 NormalZ=1 AngleXU=0 Radius=21
    g1: Circle CenterX=0 CenterY=0 CenterZ=0 NormalX=0 NormalY=0 NormalZ=1 AngleXU=0 Radius=40
    g2: Circle CenterX=0 CenterY=0 CenterZ=0 NormalX=0 NormalY=0 NormalZ=1 AngleXU=0 Radius=38.5
  constraints (6):
    c: Diameter(g0) = 42
    c: Coincident(g0,g-1)
    c: Diameter(g1) = 80
    c: Coincident(g1,g0)
    c: Coincident(g2,g0)
    c: Diameter(g2) = 77
FEATURE [App::Link] upper_cover_display
  LinkPlacement = pos=(-2.4e-15,-3.3e-15,39) rot=(0,0,-1;6.08242rad)
  LinkedObject = -> Body021
  Placement = pos=(-2.4e-15,-3.3e-15,39) rot=(0,0,-1;6.08242rad)
FEATURE [Sketcher::SketchObject] Sketch015
  ArcFitTolerance = 1e-06
  AttachmentSupport = -> [PolarPattern]
  ExternalGeometry = -> [PolarPattern]
  FullyConstrained = true
  MakeInternals = false
  MapMode = 5
  Placement = pos=(4e-15,4e-15,36) rot=(0,0,1;0rad)
  expr: Constraints[13] = 9
  sketch-geometry (5):
    g0: Circle [constr] CenterX=0 CenterY=0 CenterZ=0 NormalX=0 NormalY=0 NormalZ=1 AngleXU=0 Radius=52.0776
    g1: Circle CenterX=0 CenterY=0 CenterZ=0 NormalX=0 NormalY=0 NormalZ=1 AngleXU=0 Radius=42.5776
    g2: Circle CenterX=0 CenterY=0 CenterZ=0 NormalX=0 NormalY=0 NormalZ=1 AngleXU=0 Radius=51.5776
    g3: LineSegment [constr] StartX=-42.5776 StartY=0 StartZ=0 EndX=-42.0776 EndY=0 EndZ=0
    g4: LineSegment [constr] StartX=-52.0776 StartY=0 StartZ=0 EndX=-51.5776 EndY=0 EndZ=0
  constraints (14):
    c: Coincident(g0,g-3)
    c: PointOnObject(g-4,g0)
    c: Coincident(g1,g0)
    c: Coincident(g2,g0)
    c: PointOnObject(g3,g1)
    c: PointOnObject(g3,g-3)
    c: PointOnObject(g3,g-1)
    c: PointOnObject(g3,g-1)
    c: PointOnObject(g4,g0)
    c: PointOnObject(g4,g2)
    c: PointOnObject(g4,g-1)
    c: PointOnObject(g4,g-1)
    c: Equal(g4,g3)
    c: Distance(g2,g1) = 9
FEATURE [PartDesign::Pocket] Pocket005
  BaseFeature = -> PolarPattern
  Direction = (0,0,-1)
  Length = 3
  Length2 = 5
  Profile = -> Sketch015
  ReferenceAxis = -> Sketch015 [N_Axis]
  Refine = true
  Suppressed = false
  Type = 0
  expr: Length = 3
FEATURE [PartDesign::Fillet] Fillet003
  Base = -> Pocket005 [Edge312,Edge949]
  BaseFeature = -> Pocket005
  Radius = 1
  Refine = true
  SupportTransform = false
  Suppressed = false
  UseAllEdges = false
  expr: Radius = 1
FEATURE [Sketcher::SketchObject] Sketch016
  ArcFitTolerance = 1e-06
  AttachmentSupport = -> [Fillet003]
  ExternalGeometry = -> [Fillet003]
  FullyConstrained = false
  MakeInternals = false
  MapMode = 5
  Placement = pos=(0,0,33) rot=(0,0,1;0rad)
  sketch-geometry (8):
    g0: ArcOfCircle CenterX=4e-15 CenterY=4e-15 CenterZ=0 NormalX=0 NormalY=0 NormalZ=1 AngleXU=0 Radius=44.0776 StartAngle=1.01451 EndAngle=1.42895
    g1: ArcOfCircle CenterX=4e-15 CenterY=4e-15 CenterZ=0 NormalX=0 NormalY=0 NormalZ=1 AngleXU=0 Radius=50.0776 StartAngle=1.01451 EndAngle=1.42895
    g2: LineSegment StartX=6.23147 StartY=43.6349 StartZ=0 EndX=7.07972 EndY=49.5746 EndZ=0
    g3: LineSegment StartX=23.2744 StartY=37.4318 StartZ=0 EndX=26.4426 EndY=42.5271 EndZ=0
    g4: LineSegment [constr] StartX=23.2744 StartY=37.4318 StartZ=0 EndX=23.0104 EndY=37.0071 EndZ=0
    g5: LineSegment [constr] StartX=26.4426 StartY=42.5271 StartZ=0 EndX=26.7066 EndY=42.9517 EndZ=0
    g6: LineSegment [constr] StartX=4e-15 StartY=4e-15 StartZ=0 EndX=-40.9495 EndY=14.9044 EndZ=0
    g7: LineSegment [constr] StartX=4e-15 StartY=4e-15 StartZ=0 EndX=14.9044 EndY=40.9495 EndZ=0
  constraints (22):
    c: Coincident(g0,g-4)
    c: Coincident(g1,g0)
    c: Coincident(g2,g0)
    c: Coincident(g2,g1)
    c: Coincident(g3,g0)
    c: Coincident(g3,g1)
    c: Equal(g2,g3)
    c: Perpendicular(g0,g2)
    c: Coincident(g4,g0)
    c: PointOnObject(g4,g-4)
    c: Coincident(g5,g1)
    c: PointOnObject(g5,g-3)
    c: Parallel(g4,g3)
    c: Parallel(g3,g5)
    c: Equal(g5,g4)
    c: Distance(g3,g3) = 6
    c: Coincident(g6,g0)
    c: Angle(g6,g-1) = 0.349066
    c: PointOnObject(g6,g-4)
    c: Coincident(g7,g0)
    c: Perpendicular(g6,g7)
    c: Equal(g7,g6)
FEATURE [PartDesign::Pad] Pad004
  BaseFeature = -> Fillet003
  Direction = (0,0,1)
  Length = 1.5
  Length2 = 10
  Profile = -> Sketch016
  ReferenceAxis = -> Sketch016 [N_Axis]
  Refine = true
  Suppressed = false
  Type = 0
  expr: Length = 1.5
FEATURE [PartDesign::PolarPattern] PolarPattern002
  Angle = 360
  Axis = -> Sketch016 [N_Axis]
  BaseFeature = -> Pad004
  Mode = 0
  Occurrences = 2
  Offset = 120
  Originals = -> [Pad004]
  Refine = true
  Suppressed = false
  TransformMode = 0
FEATURE [PartDesign::Fillet] Fillet004
  Base = -> PolarPattern002 [Face177,Face175]
  BaseFeature = -> PolarPattern002
  Radius = 1
  Refine = true
  SupportTransform = false
  Suppressed = false
  UseAllEdges = false
FEATURE [PartDesign::Body] Body016  label="outer_gear"
  AllowCompound = false
  Group = -> [InternalInvoluteGear,Sketch010,Revolution001,Sketch011,Revolution002,PolarPattern,Sketch015,Pocket005,Fillet003,Sketch016,Pad004,PolarPattern002,Fillet004]
  Origin = -> Origin026
  Placement = pos=(0,0,41) rot=(0,0,1;0rad)
  Tip = -> Fillet004
FEATURE [PartDesign::Pad] Pad005
  Direction = (0,0,1)
  Length = 3
  Length2 = 10
  Profile = -> Sketch012 [Edge2,Edge1]
  ReferenceAxis = -> Sketch012 [N_Axis]
  Refine = true
  Suppressed = false
  Type = 0
  expr: Length = 3
FEATURE [Sketcher::SketchObject] Sketch017
  ArcFitTolerance = 1e-06
  FullyConstrained = true
  MakeInternals = false
  MapMode = 5
  Placement = pos=(40,0,0) rot=(1,0,0;1.5708rad)
  expr: Constraints[4] = 14
  sketch-geometry (6):
    g0: LineSegment StartX=5.78797 StartY=-27 StartZ=0 EndX=5.78797 EndY=-13 EndZ=0
    g1: LineSegment StartX=5.78797 StartY=-13 StartZ=0 EndX=0 EndY=0 EndZ=0
    g2: LineSegment StartX=0 StartY=0 StartZ=0 EndX=-1.5 EndY=0 EndZ=0
    g3: LineSegment StartX=-1.5 StartY=0 StartZ=0 EndX=4.28797 EndY=-13 EndZ=0
    g4: LineSegment StartX=4.28797 StartY=-13 StartZ=0 EndX=4.28797 EndY=-27 EndZ=0
    g5: LineSegment StartX=4.28797 StartY=-27 StartZ=0 EndX=5.78797 EndY=-27 EndZ=0
  constraints (17):
    c: Vertical(g0)
    c: Coincident(g1,g0)
    c: Coincident(g1,g-1)
    c: Angle(g0,g1) = 0.418879
    c: DistanceY(g0,g0) = 14
    c: DistanceY(g0,g1) = 27
    c: Coincident(g2,g1)
    c: PointOnObject(g2,g-1)
    c: Coincident(g2,g3)
    c: Coincident(g3,g4)
    c: Vertical(g4)
    c: Coincident(g4,g5)
    c: Coincident(g5,g0)
    c: Perpendicular(g4,g5)
    c: Equal(g3,g1)
    c: Parallel(g3,g1)
    c: DistanceX(g5,g5) = 1.5
FEATURE [PartDesign::Revolution] Revolution003
  Angle = 360
  Angle2 = 60
  Axis = (1e-16,1e-16,1)
  Base = (0,0,0)
  BaseFeature = -> Pad005
  Profile = -> Sketch017
  ReferenceAxis = -> Z_Axis017
  Refine = true
  Reversed = true
  Suppressed = false
  Type = 0
FEATURE [PartDesign::Chamfer] Chamfer
  Angle = 45
  Base = -> Revolution003 [Edge13,Edge10]
  BaseFeature = -> Revolution003
  ChamferType = 0
  FlipDirection = false
  Refine = true
  Size = 2
  Size2 = 1
  SupportTransform = false
  Suppressed = false
  UseAllEdges = false
FEATURE [Sketcher::SketchObject] Sketch018
  ArcFitTolerance = 1e-06
  FullyConstrained = true
  MakeInternals = false
  MapMode = 5
  Placement = pos=(44.288,-6.1e-15,-27) rot=(0,0.707107,0.707107;3.14159rad)
  sketch-geometry (4):
    g0: LineSegment StartX=0 StartY=0 StartZ=0 EndX=0 EndY=5.12132 EndZ=0
    g1: LineSegment StartX=0 StartY=5.12132 StartZ=0 EndX=2.12132 EndY=3 EndZ=0
    g2: LineSegment StartX=2.12132 StartY=3 StartZ=0 EndX=2.12132 EndY=0 EndZ=0
    g3: LineSegment StartX=2.12132 StartY=0 StartZ=0 EndX=0 EndY=0 EndZ=0
  constraints (11):
    c: Coincident(g-1,g0)
    c: Vertical(g0)
    c: Coincident(g0,g1)
    c: Coincident(g1,g2)
    c: PointOnObject(g2,g-1)
    c: Vertical(g2)
    c: Coincident(g2,g3)
    c: Coincident(g3,g0)
    c: Angle(g2,g1) = 0.785398
    c: Equal(g2,g1)
    c: DistanceY(g2,g2) = 3
FEATURE [PartDesign::Revolution] Revolution004
  Angle = 9
  Angle2 = 60
  Axis = (1e-16,1e-16,1)
  Base = (0,0,0)
  BaseFeature = -> Chamfer
  Profile = -> Sketch018
  ReferenceAxis = -> Z_Axis017
  Refine = true
  Suppressed = false
  Type = 0
  expr: Angle = 9
FEATURE [PartDesign::PolarPattern] PolarPattern003
  Angle = 360
  Axis = -> Z_Axis017
  BaseFeature = -> Revolution004
  Mode = 0
  Occurrences = 4
  Offset = 120
  Originals = -> [Revolution004]
  Refine = true
  Suppressed = false
  TransformMode = 0
FEATURE [Sketcher::SketchObject] Sketch019
  ArcFitTolerance = 1e-06
  AttachmentSupport = -> [Fillet]
  FullyConstrained = true
  MakeInternals = false
  MapMode = 5
  Placement = pos=(0,0,12) rot=(0,0,1;0rad)
  sketch-geometry (1):
    g0: Circle CenterX=0 CenterY=0 CenterZ=0 NormalX=0 NormalY=0 NormalZ=1 AngleXU=0 Radius=44
  constraints (2):
    c: Diameter(g0) = 88
    c: Coincident(g0,g-1)
FEATURE [Sketcher::SketchObject] Sketch020
  ArcFitTolerance = 1e-06
  FullyConstrained = true
  MakeInternals = false
  MapMode = 5
  Placement = pos=(44,0,12) rot=(1,0,0;1.5708rad)
  sketch-geometry (9):
    g0: LineSegment StartX=-2.19203 StartY=0 StartZ=0 EndX=-2.19203 EndY=3.1 EndZ=0
    g1: LineSegment StartX=-2.19203 StartY=3.1 StartZ=0 EndX=0 EndY=5.29203 EndZ=0
    g2: LineSegment StartX=0 StartY=5.29203 StartZ=0 EndX=0 EndY=7.79203 EndZ=0
    g3: LineSegment StartX=-5.9535 StartY=0 StartZ=0 EndX=-2.19203 EndY=0 EndZ=0
    g4: LineSegment StartX=0 StartY=7.79203 StartZ=0 EndX=-3.44203 EndY=4.35 EndZ=0
    g5: LineSegment StartX=-3.44203 StartY=4.35 StartZ=0 EndX=-5.9535 EndY=0 EndZ=0
    g6: LineSegment [constr] StartX=-3.44203 StartY=4.35 StartZ=0 EndX=-2.19203 EndY=3.1 EndZ=0
    g7: LineSegment StartX=-2.19203 StartY=0 StartZ=0 EndX=0 EndY=0 EndZ=0
    g8: LineSegment StartX=0 StartY=0 StartZ=0 EndX=0 EndY=5.29203 EndZ=0
  constraints (24):
    c: PointOnObject(g0,g-1)
    c: Vertical(g0)
    c: Coincident(g0,g1)
    c: PointOnObject(g1,g-2)
    c: Coincident(g1,g2)
    c: Coincident(g3,g0)
    c: PointOnObject(g3,g-1)
    c: PointOnObject(g2,g-2)
    c: Angle(g1,g0) = 0.785398
    c: DistanceY(g0,g0) = 3.1
    c: Equal(g1,g0)
    c: DistanceY(g2,g2) = 2.5
    c: Coincident(g2,g4)
    c: Coincident(g4,g5)
    c: Coincident(g3,g5)
    c: Angle(g3,g5) = 1.0472
    c: Parallel(g4,g1)
    c: Coincident(g6,g4)
    c: Coincident(g6,g0)
    c: Perpendicular(g4,g6)
    c: Coincident(g7,g0)
    c: Coincident(g7,g-1)
    c: Coincident(g8,g7)
    c: Coincident(g8,g1)
FEATURE [PartDesign::Revolution] Revolution005
  Angle = 323
  Angle2 = 47
  Axis = (1e-16,1e-16,1)
  Base = (0,0,0)
  BaseFeature = -> Fillet
  Profile = -> Sketch020 [Edge4,Edge5,Edge2,Edge1,Edge3,Edge6]
  ReferenceAxis = -> Z_Axis003
  Refine = true
  Reversed = true
  Suppressed = false
  Type = 4
  expr: Angle = 323
  expr: Angle2 = 47
FEATURE [PartDesign::Revolution] Revolution006
  Angle = 313
  Angle2 = 53
  Axis = (1e-16,1e-16,1)
  Base = (0,0,0)
  BaseFeature = -> Revolution005
  Profile = -> Sketch020 [Edge8,Edge3,Edge4,Edge5,Edge6,Edge7]
  ReferenceAxis = -> Z_Axis003
  Refine = true
  Reversed = true
  Suppressed = false
  Type = 4
  expr: Angle = 313
  expr: Angle2 = 53
FEATURE [PartDesign::PolarPattern] PolarPattern004
  Angle = 360
  Axis = -> Z_Axis003
  BaseFeature = -> Revolution006
  Mode = 0
  Occurrences = 4
  Offset = 120
  Originals = -> [Revolution005,Revolution006]
  Refine = true
  Suppressed = false
  TransformMode = 0
  expr: Occurrences = 4
FEATURE [PartDesign::Fillet] Fillet005
  Base = -> PolarPattern004 [Face5]
  BaseFeature = -> PolarPattern004
  Radius = 0.5
  Refine = true
  SupportTransform = false
  Suppressed = false
  UseAllEdges = false
  expr: Radius = 0.5
FEATURE [PartDesign::Fillet] Fillet006
  Base = -> Fillet005 [?Face21,Face20]
  BaseFeature = -> Fillet005
  Radius = 0.5
  Refine = true
  SupportTransform = false
  Suppressed = false
  UseAllEdges = false
  expr: Radius = 0.5
FEATURE [PartDesign::Fillet] Fillet007
  Base = -> Fillet006 [Face29,Face32]
  BaseFeature = -> Fillet006
  Radius = 0.5
  Refine = true
  SupportTransform = false
  Suppressed = false
  UseAllEdges = false
FEATURE [PartDesign::Fillet] Fillet008
  Base = -> Fillet007 [Face44,Face41]
  BaseFeature = -> Fillet007
  Radius = 0.5
  Refine = true
  SupportTransform = false
  Suppressed = false
  UseAllEdges = false
FEATURE [PartDesign::Fillet] Fillet009
  Base = -> PolarPattern003 [Face21,Face22,Face23,Face7]
  BaseFeature = -> PolarPattern003
  Radius = 0.5
  Refine = true
  SupportTransform = false
  Suppressed = false
  UseAllEdges = false
  expr: Radius = 0.5
FEATURE [PartDesign::Body] Body021  label="upper_cover_display"
  AllowCompound = false
  Group = -> [Sketch012,Pad005,Sketch017,Revolution003,Chamfer,Sketch018,Revolution004,PolarPattern003,Fillet009]
  Origin = -> Origin034
  Tip = -> Fillet009
FEATURE [Sketcher::SketchObject] Sketch021
  ArcFitTolerance = 1e-06
  AttachmentSupport = -> [Origin036]
  FullyConstrained = true
  MakeInternals = false
  MapMode = 5
  expr: Constraints[2] = 42.75 * 2
  expr: Constraints[3] = 51 * 2
  sketch-geometry (2):
    g0: Circle CenterX=0 CenterY=0 CenterZ=0 NormalX=0 NormalY=0 NormalZ=1 AngleXU=0 Radius=42.75
    g1: Circle CenterX=0 CenterY=0 CenterZ=0 NormalX=0 NormalY=0 NormalZ=1 AngleXU=0 Radius=51
  constraints (4):
    c: Coincident(g0,g-1)
    c: Coincident(g1,g0)
    c: Diameter(g0) = 85.5
    c: Diameter(g1) = 102
FEATURE [PartDesign::Pad] Pad006
  Direction = (0,0,1)
  Length = 3
  Length2 = 10
  Profile = -> Sketch021
  ReferenceAxis = -> Sketch021 [N_Axis]
  Refine = true
  Suppressed = false
  Type = 0
  expr: Length = 3
FEATURE [Sketcher::SketchObject] Sketch022
  ArcFitTolerance = 1e-06
  AttachmentSupport = -> [Pad006]
  FullyConstrained = false
  MakeInternals = false
  MapMode = 5
  Placement = pos=(0,0,3) rot=(0,0,1;0rad)
  sketch-geometry (4):
    g0: ArcOfCircle CenterX=0 CenterY=0 CenterZ=0 NormalX=0 NormalY=0 NormalZ=1 AngleXU=0 Radius=44.08 StartAngle=1.00282 EndAngle=1.41716
    g1: ArcOfCircle CenterX=0 CenterY=0 CenterZ=0 NormalX=0 NormalY=0 NormalZ=1 AngleXU=0 Radius=50.08 StartAngle=1.00282 EndAngle=1.41716
    g2: LineSegment StartX=6.74568 StartY=43.5608 StartZ=0 EndX=7.66388 EndY=49.4901 EndZ=0
    g3: LineSegment StartX=23.7119 StartY=37.159 StartZ=0 EndX=26.9394 EndY=42.217 EndZ=0
  constraints (11):
    c: Coincident(g1,g0)
    c: Coincident(g2,g0)
    c: Coincident(g2,g1)
    c: Coincident(g3,g0)
    c: Coincident(g3,g1)
    c: Equal(g2,g3)
    c: Perpendicular(g0,g2)
    c: Distance(g3,g3) = 6
    c: Radius(g0) = 44.08
    c: Angle(g0) = 0.414341
    c: Coincident(g0,g-1)
FEATURE [PartDesign::Pocket] Pocket006
  BaseFeature = -> Pad006
  Direction = (0,0,-1)
  Length = 1.5
  Length2 = 5
  Profile = -> Sketch022
  ReferenceAxis = -> Sketch022 [N_Axis]
  Refine = true
  Suppressed = false
  Type = 0
  expr: Length = 1.5
FEATURE [PartDesign::PolarPattern] PolarPattern005
  Angle = 360
  Axis = -> Sketch022 [N_Axis]
  BaseFeature = -> Pocket006
  Mode = 0
  Occurrences = 2
  Offset = 120
  Originals = -> [Pocket006]
  Refine = true
  Suppressed = false
  TransformMode = 0
FEATURE [PartDesign::Fillet] Fillet010
  Base = -> PolarPattern005 [Face2]
  BaseFeature = -> PolarPattern005
  Radius = 0.3
  Refine = true
  SupportTransform = false
  Suppressed = false
  UseAllEdges = false
  expr: Radius = 0.3
FEATURE [PartDesign::Fillet] Fillet011
  Base = -> Fillet010 [Face3]
  BaseFeature = -> Fillet010
  Radius = 0.4
  Refine = true
  SupportTransform = false
  Suppressed = false
  UseAllEdges = false
  expr: Radius = 0.4
FEATURE [Sketcher::SketchObject] Sketch023
  ArcFitTolerance = 1e-06
  AttachmentSupport = -> [Fillet011]
  FullyConstrained = false
  MakeInternals = false
  MapMode = 5
  Placement = pos=(0,0,0) rot=(1,0,0;3.14159rad)
  sketch-geometry (1190):
    g0: BSplineCurve PolesCount=2 KnotsCount=2 Degree=1 IsPeriodic=0
    g1: BSplineCurve PolesCount=2 KnotsCount=2 Degree=1 IsPeriodic=0
    g2: BSplineCurve PolesCount=2 KnotsCount=2 Degree=1 IsPeriodic=0
    g3: BSplineCurve PolesCount=2 KnotsCount=2 Degree=1 IsPeriodic=0
    g4: BSplineCurve PolesCount=2 KnotsCount=2 Degree=1 IsPeriodic=0
    g5: BSplineCurve PolesCount=2 KnotsCount=2 Degree=1 IsPeriodic=0
    g6: BSplineCurve PolesCount=2 KnotsCount=2 Degree=1 IsPeriodic=0
    g7: BSplineCurve PolesCount=2 KnotsCount=2 Degree=1 IsPeriodic=0
    g8: BSplineCurve PolesCount=2 KnotsCount=2 Degree=1 IsPeriodic=0
    g9: BSplineCurve PolesCount=2 KnotsCount=2 Degree=1 IsPeriodic=0
    g10: BSplineCurve PolesCount=2 KnotsCount=2 Degree=1 IsPeriodic=0
    g11: BSplineCurve PolesCount=2 KnotsCount=2 Degree=1 IsPeriodic=0
    g12: BSplineCurve PolesCount=2 KnotsCount=2 Degree=1 IsPeriodic=0
    g13: BSplineCurve PolesCount=2 KnotsCount=2 Degree=1 IsPeriodic=0
    g14: BSplineCurve PolesCount=2 KnotsCount=2 Degree=1 IsPeriodic=0
    g15: BSplineCurve PolesCount=2 KnotsCount=2 Degree=1 IsPeriodic=0
    g16: BSplineCurve PolesCount=2 KnotsCount=2 Degree=1 IsPeriodic=0
    g17: BSplineCurve PolesCount=2 KnotsCount=2 Degree=1 IsPeriodic=0
    g18: BSplineCurve PolesCount=2 KnotsCount=2 Degree=1 IsPeriodic=0
    g19: BSplineCurve PolesCount=2 KnotsCount=2 Degree=1 IsPeriodic=0
    g20: BSplineCurve PolesCount=2 KnotsCount=2 Degree=1 IsPeriodic=0
    g21: BSplineCurve PolesCount=2 KnotsCount=2 Degree=1 IsPeriodic=0
    g22: BSplineCurve PolesCount=2 KnotsCount=2 Degree=1 IsPeriodic=0
    g23: BSplineCurve PolesCount=2 KnotsCount=2 Degree=1 IsPeriodic=0
    g24: BSplineCurve PolesCount=2 KnotsCount=2 Degree=1 IsPeriodic=0
    g25: BSplineCurve PolesCount=2 KnotsCount=2 Degree=1 IsPeriodic=0
    g26: BSplineCurve PolesCount=2 KnotsCount=2 Degree=1 IsPeriodic=0
    g27: BSplineCurve PolesCount=2 KnotsCount=2 Degree=1 IsPeriodic=0
    g28: BSplineCurve PolesCount=2 KnotsCount=2 Degree=1 IsPeriodic=0
    g29: BSplineCurve PolesCount=2 KnotsCount=2 Degree=1 IsPeriodic=0
    g30: BSplineCurve PolesCount=2 KnotsCount=2 Degree=1 IsPeriodic=0
    g31: BSplineCurve PolesCount=2 KnotsCount=2 Degree=1 IsPeriodic=0
    g32: BSplineCurve PolesCount=2 KnotsCount=2 Degree=1 IsPeriodic=0
    g33: BSplineCurve PolesCount=2 KnotsCount=2 Degree=1 IsPeriodic=0
    g34: BSplineCurve PolesCount=2 KnotsCount=2 Degree=1 IsPeriodic=0
    g35: BSplineCurve PolesCount=2 KnotsCount=2 Degree=1 IsPeriodic=0
    g36: BSplineCurve PolesCount=2 KnotsCount=2 Degree=1 IsPeriodic=0
    g37: BSplineCurve PolesCount=2 KnotsCount=2 Degree=1 IsPeriodic=0
    g38: BSplineCurve PolesCount=2 KnotsCount=2 Degree=1 IsPeriodic=0
    g39: BSplineCurve PolesCount=2 KnotsCount=2 Degree=1 IsPeriodic=0
    g40: BSplineCurve PolesCount=2 KnotsCount=2 Degree=1 IsPeriodic=0
    g41: BSplineCurve PolesCount=2 KnotsCount=2 Degree=1 IsPeriodic=0
    g42: BSplineCurve PolesCount=2 KnotsCount=2 Degree=1 IsPeriodic=0
    g43: BSplineCurve PolesCount=2 KnotsCount=2 Degree=1 IsPeriodic=0
    g44: BSplineCurve PolesCount=2 KnotsCount=2 Degree=1 IsPeriodic=0
    g45: BSplineCurve PolesCount=2 KnotsCount=2 Degree=1 IsPeriodic=0
    g46: BSplineCurve PolesCount=2 KnotsCount=2 Degree=1 IsPeriodic=0
    g47: BSplineCurve PolesCount=2 KnotsCount=2 Degree=1 IsPeriodic=0
    g48: BSplineCurve PolesCount=2 KnotsCount=2 Degree=1 IsPeriodic=0
    g49: BSplineCurve PolesCount=2 KnotsCount=2 Degree=1 IsPeriodic=0
    g50: BSplineCurve PolesCount=2 KnotsCount=2 Degree=1 IsPeriodic=0
    g51: BSplineCurve PolesCount=2 KnotsCount=2 Degree=1 IsPeriodic=0
    g52: BSplineCurve PolesCount=2 KnotsCount=2 Degree=1 IsPeriodic=0
    g53: BSplineCurve PolesCount=2 KnotsCount=2 Degree=1 IsPeriodic=0
    g54: BSplineCurve PolesCount=2 KnotsCount=2 Degree=1 IsPeriodic=0
    g55: BSplineCurve PolesCount=2 KnotsCount=2 Degree=1 IsPeriodic=0
    g56: BSplineCurve PolesCount=2 KnotsCount=2 Degree=1 IsPeriodic=0
    g57: BSplineCurve PolesCount=2 KnotsCount=2 Degree=1 IsPeriodic=0
    g58: BSplineCurve PolesCount=2 KnotsCount=2 Degree=1 IsPeriodic=0
    g59: BSplineCurve PolesCount=2 KnotsCount=2 Degree=1 IsPeriodic=0
    g60: BSplineCurve PolesCount=2 KnotsCount=2 Degree=1 IsPeriodic=0
    g61: BSplineCurve PolesCount=2 KnotsCount=2 Degree=1 IsPeriodic=0
    g62: BSplineCurve PolesCount=2 KnotsCount=2 Degree=1 IsPeriodic=0
    g63: BSplineCurve PolesCount=2 KnotsCount=2 Degree=1 IsPeriodic=0
    g64: BSplineCurve PolesCount=2 KnotsCount=2 Degree=1 IsPeriodic=0
    g65: BSplineCurve PolesCount=2 KnotsCount=2 Degree=1 IsPeriodic=0
    g66: BSplineCurve PolesCount=2 KnotsCount=2 Degree=1 IsPeriodic=0
    g67: BSplineCurve PolesCount=2 KnotsCount=2 Degree=1 IsPeriodic=0
    g68: BSplineCurve PolesCount=2 KnotsCount=2 Degree=1 IsPeriodic=0
    g69: BSplineCurve PolesCount=2 KnotsCount=2 Degree=1 IsPeriodic=0
    g70: BSplineCurve PolesCount=2 KnotsCount=2 Degree=1 IsPeriodic=0
    g71: BSplineCurve PolesCount=2 KnotsCount=2 Degree=1 IsPeriodic=0
    g72: BSplineCurve PolesCount=2 KnotsCount=2 Degree=1 IsPeriodic=0
    g73: BSplineCurve PolesCount=2 KnotsCount=2 Degree=1 IsPeriodic=0
    g74: BSplineCurve PolesCount=2 KnotsCount=2 Degree=1 IsPeriodic=0
    g75: BSplineCurve PolesCount=2 KnotsCount=2 Degree=1 IsPeriodic=0
    g76: BSplineCurve PolesCount=2 KnotsCount=2 Degree=1 IsPeriodic=0
    g77: BSplineCurve PolesCount=2 KnotsCount=2 Degree=1 IsPeriodic=0
    g78: BSplineCurve PolesCount=2 KnotsCount=2 Degree=1 IsPeriodic=0
    g79: BSplineCurve PolesCount=2 KnotsCount=2 Degree=1 IsPeriodic=0
    g80: BSplineCurve PolesCount=2 KnotsCount=2 Degree=1 IsPeriodic=0
    g81: BSplineCurve PolesCount=2 KnotsCount=2 Degree=1 IsPeriodic=0
    g82: BSplineCurve PolesCount=2 KnotsCount=2 Degree=1 IsPeriodic=0
    g83: BSplineCurve PolesCount=2 KnotsCount=2 Degree=1 IsPeriodic=0
    g84: BSplineCurve PolesCount=2 KnotsCount=2 Degree=1 IsPeriodic=0
    g85: BSplineCurve PolesCount=2 KnotsCount=2 Degree=1 IsPeriodic=0
    g86: BSplineCurve PolesCount=2 KnotsCount=2 Degree=1 IsPeriodic=0
    g87: BSplineCurve PolesCount=2 KnotsCount=2 Degree=1 IsPeriodic=0
    g88: BSplineCurve PolesCount=2 KnotsCount=2 Degree=1 IsPeriodic=0
    g89: BSplineCurve PolesCount=2 KnotsCount=2 Degree=1 IsPeriodic=0
    g90: BSplineCurve PolesCount=2 KnotsCount=2 Degree=1 IsPeriodic=0
    g91: BSplineCurve PolesCount=2 KnotsCount=2 Degree=1 IsPeriodic=0
    g92: BSplineCurve PolesCount=2 KnotsCount=2 Degree=1 IsPeriodic=0
    g93: BSplineCurve PolesCount=2 KnotsCount=2 Degree=1 IsPeriodic=0
    g94: BSplineCurve PolesCount=2 KnotsCount=2 Degree=1 IsPeriodic=0
    g95: BSplineCurve PolesCount=2 KnotsCount=2 Degree=1 IsPeriodic=0
    g96: BSplineCurve PolesCount=2 KnotsCount=2 Degree=1 IsPeriodic=0
    g97: BSplineCurve PolesCount=2 KnotsCount=2 Degree=1 IsPeriodic=0
    g98: BSplineCurve PolesCount=2 KnotsCount=2 Degree=1 IsPeriodic=0
    g99: BSplineCurve PolesCount=2 KnotsCount=2 Degree=1 IsPeriodic=0
    g100: BSplineCurve PolesCount=2 KnotsCount=2 Degree=1 IsPeriodic=0
    g101: BSplineCurve PolesCount=2 KnotsCount=2 Degree=1 IsPeriodic=0
    g102: BSplineCurve PolesCount=2 KnotsCount=2 Degree=1 IsPeriodic=0
    g103: BSplineCurve PolesCount=2 KnotsCount=2 Degree=1 IsPeriodic=0
    g104: BSplineCurve PolesCount=2 KnotsCount=2 Degree=1 IsPeriodic=0
    g105: BSplineCurve PolesCount=2 KnotsCount=2 Degree=1 IsPeriodic=0
    g106: BSplineCurve PolesCount=2 KnotsCount=2 Degree=1 IsPeriodic=0
    g107: BSplineCurve PolesCount=2 KnotsCount=2 Degree=1 IsPeriodic=0
    g108: BSplineCurve PolesCount=2 KnotsCount=2 Degree=1 IsPeriodic=0
    g109: BSplineCurve PolesCount=2 KnotsCount=2 Degree=1 IsPeriodic=0
    g110: BSplineCurve PolesCount=2 KnotsCount=2 Degree=1 IsPeriodic=0
    g111: BSplineCurve PolesCount=2 KnotsCount=2 Degree=1 IsPeriodic=0
    g112: BSplineCurve PolesCount=2 KnotsCount=2 Degree=1 IsPeriodic=0
    g113: BSplineCurve PolesCount=2 KnotsCount=2 Degree=1 IsPeriodic=0
    g114: BSplineCurve PolesCount=2 KnotsCount=2 Degree=1 IsPeriodic=0
    g115: BSplineCurve PolesCount=2 KnotsCount=2 Degree=1 IsPeriodic=0
    g116: BSplineCurve PolesCount=2 KnotsCount=2 Degree=1 IsPeriodic=0
    g117: BSplineCurve PolesCount=2 KnotsCount=2 Degree=1 IsPeriodic=0
    g118: BSplineCurve PolesCount=2 KnotsCount=2 Degree=1 IsPeriodic=0
    g119: BSplineCurve PolesCount=2 KnotsCount=2 Degree=1 IsPeriodic=0
    g120: BSplineCurve PolesCount=2 KnotsCount=2 Degree=1 IsPeriodic=0
    g121: BSplineCurve PolesCount=2 KnotsCount=2 Degree=1 IsPeriodic=0
    g122: BSplineCurve PolesCount=2 KnotsCount=2 Degree=1 IsPeriodic=0
    g123: BSplineCurve PolesCount=2 KnotsCount=2 Degree=1 IsPeriodic=0
    g124: BSplineCurve PolesCount=2 KnotsCount=2 Degree=1 IsPeriodic=0
    g125: BSplineCurve PolesCount=2 KnotsCount=2 Degree=1 IsPeriodic=0
    g126: BSplineCurve PolesCount=2 KnotsCount=2 Degree=1 IsPeriodic=0
    g127: BSplineCurve PolesCount=2 KnotsCount=2 Degree=1 IsPeriodic=0
    g128: BSplineCurve PolesCount=3 KnotsCount=2 Degree=2 IsPeriodic=0
    g129: BSplineCurve PolesCount=3 KnotsCount=2 Degree=2 IsPeriodic=0
    g130: BSplineCurve PolesCount=3 KnotsCount=2 Degree=2 IsPeriodic=0
    g131: BSplineCurve PolesCount=3 KnotsCount=2 Degree=2 IsPeriodic=0
    g132: BSplineCurve PolesCount=3 KnotsCount=2 Degree=2 IsPeriodic=0
    g133: BSplineCurve PolesCount=3 KnotsCount=2 Degree=2 IsPeriodic=0
    g134: BSplineCurve PolesCount=3 KnotsCount=2 Degree=2 IsPeriodic=0
    g135: BSplineCurve PolesCount=3 KnotsCount=2 Degree=2 IsPeriodic=0
    g136: BSplineCurve PolesCount=3 KnotsCount=2 Degree=2 IsPeriodic=0
    g137: BSplineCurve PolesCount=3 KnotsCount=2 Degree=2 IsPeriodic=0
    g138: BSplineCurve PolesCount=3 KnotsCount=2 Degree=2 IsPeriodic=0
    g139: BSplineCurve PolesCount=3 KnotsCount=2 Degree=2 IsPeriodic=0
    g140: BSplineCurve PolesCount=3 KnotsCount=2 Degree=2 IsPeriodic=0
    g141: BSplineCurve PolesCount=3 KnotsCount=2 Degree=2 IsPeriodic=0
    g142: BSplineCurve PolesCount=3 KnotsCount=2 Degree=2 IsPeriodic=0
    g143: BSplineCurve PolesCount=3 KnotsCount=2 Degree=2 IsPeriodic=0
    g144: BSplineCurve PolesCount=2 KnotsCount=2 Degree=1 IsPeriodic=0
    g145: BSplineCurve PolesCount=2 KnotsCount=2 Degree=1 IsPeriodic=0
    g146: BSplineCurve PolesCount=2 KnotsCount=2 Degree=1 IsPeriodic=0
    g147: BSplineCurve PolesCount=2 KnotsCount=2 Degree=1 IsPeriodic=0
    g148: BSplineCurve PolesCount=2 KnotsCount=2 Degree=1 IsPeriodic=0
    g149: BSplineCurve PolesCount=2 KnotsCount=2 Degree=1 IsPeriodic=0
    g150: BSplineCurve PolesCount=2 KnotsCount=2 Degree=1 IsPeriodic=0
    g151: BSplineCurve PolesCount=2 KnotsCount=2 Degree=1 IsPeriodic=0
    g152: BSplineCurve PolesCount=2 KnotsCount=2 Degree=1 IsPeriodic=0
    g153: BSplineCurve PolesCount=2 KnotsCount=2 Degree=1 IsPeriodic=0
    g154: BSplineCurve PolesCount=2 KnotsCount=2 Degree=1 IsPeriodic=0
    g155: BSplineCurve PolesCount=2 KnotsCount=2 Degree=1 IsPeriodic=0
    g156: BSplineCurve PolesCount=3 KnotsCount=2 Degree=2 IsPeriodic=0
    g157: BSplineCurve PolesCount=3 KnotsCount=2 Degree=2 IsPeriodic=0
    g158: BSplineCurve PolesCount=3 KnotsCount=2 Degree=2 IsPeriodic=0
    g159: BSplineCurve PolesCount=3 KnotsCount=2 Degree=2 IsPeriodic=0
    g160: BSplineCurve PolesCount=3 KnotsCount=2 Degree=2 IsPeriodic=0
    g161: BSplineCurve PolesCount=3 KnotsCount=2 Degree=2 IsPeriodic=0
    g162: BSplineCurve PolesCount=3 KnotsCount=2 Degree=2 IsPeriodic=0
    g163: BSplineCurve PolesCount=3 KnotsCount=2 Degree=2 IsPeriodic=0
    g164: BSplineCurve PolesCount=3 KnotsCount=2 Degree=2 IsPeriodic=0
    g165: BSplineCurve PolesCount=3 KnotsCount=2 Degree=2 IsPeriodic=0
    g166: BSplineCurve PolesCount=2 KnotsCount=2 Degree=1 IsPeriodic=0
    g167: BSplineCurve PolesCount=3 KnotsCount=2 Degree=2 IsPeriodic=0
    g168: BSplineCurve PolesCount=3 KnotsCount=2 Degree=2 IsPeriodic=0
    g169: BSplineCurve PolesCount=3 KnotsCount=2 Degree=2 IsPeriodic=0
    g170: BSplineCurve PolesCount=3 KnotsCount=2 Degree=2 IsPeriodic=0
    g171: BSplineCurve PolesCount=3 KnotsCount=2 Degree=2 IsPeriodic=0
    g172: BSplineCurve PolesCount=3 KnotsCount=2 Degree=2 IsPeriodic=0
    g173: BSplineCurve PolesCount=3 KnotsCount=2 Degree=2 IsPeriodic=0
    g174: BSplineCurve PolesCount=3 KnotsCount=2 Degree=2 IsPeriodic=0
    g175: BSplineCurve PolesCount=3 KnotsCount=2 Degree=2 IsPeriodic=0
    g176: BSplineCurve PolesCount=2 KnotsCount=2 Degree=1 IsPeriodic=0
    g177: BSplineCurve PolesCount=2 KnotsCount=2 Degree=1 IsPeriodic=0
    g178: BSplineCurve PolesCount=2 KnotsCount=2 Degree=1 IsPeriodic=0
    g179: BSplineCurve PolesCount=3 KnotsCount=2 Degree=2 IsPeriodic=0
    g180: BSplineCurve PolesCount=3 KnotsCount=2 Degree=2 IsPeriodic=0
    g181: BSplineCurve PolesCount=3 KnotsCount=2 Degree=2 IsPeriodic=0
    g182: BSplineCurve PolesCount=3 KnotsCount=2 Degree=2 IsPeriodic=0
    g183: BSplineCurve PolesCount=2 KnotsCount=2 Degree=1 IsPeriodic=0
    g184: BSplineCurve PolesCount=3 KnotsCount=2 Degree=2 IsPeriodic=0
    g185: BSplineCurve PolesCount=3 KnotsCount=2 Degree=2 IsPeriodic=0
    g186: BSplineCurve PolesCount=3 KnotsCount=2 Degree=2 IsPeriodic=0
    g187: BSplineCurve PolesCount=3 KnotsCount=2 Degree=2 IsPeriodic=0
    g188: BSplineCurve PolesCount=3 KnotsCount=2 Degree=2 IsPeriodic=0
    g189: BSplineCurve PolesCount=2 KnotsCount=2 Degree=1 IsPeriodic=0
    g190: BSplineCurve PolesCount=2 KnotsCount=2 Degree=1 IsPeriodic=0
    g191: BSplineCurve PolesCount=2 KnotsCount=2 Degree=1 IsPeriodic=0
    g192: BSplineCurve PolesCount=3 KnotsCount=2 Degree=2 IsPeriodic=0
    g193: BSplineCurve PolesCount=3 KnotsCount=2 Degree=2 IsPeriodic=0
    g194: BSplineCurve PolesCount=3 KnotsCount=2 Degree=2 IsPeriodic=0
    g195: BSplineCurve PolesCount=3 KnotsCount=2 Degree=2 IsPeriodic=0
    g196: BSplineCurve PolesCount=3 KnotsCount=2 Degree=2 IsPeriodic=0
    g197: BSplineCurve PolesCount=3 KnotsCount=2 Degree=2 IsPeriodic=0
    g198: BSplineCurve PolesCount=2 KnotsCount=2 Degree=1 IsPeriodic=0
    g199: BSplineCurve PolesCount=3 KnotsCount=2 Degree=2 IsPeriodic=0
    g200: BSplineCurve PolesCount=3 KnotsCount=2 Degree=2 IsPeriodic=0
    g201: BSplineCurve PolesCount=3 KnotsCount=2 Degree=2 IsPeriodic=0
    g202: BSplineCurve PolesCount=3 KnotsCount=2 Degree=2 IsPeriodic=0
    g203: BSplineCurve PolesCount=3 KnotsCount=2 Degree=2 IsPeriodic=0
    g204: BSplineCurve PolesCount=3 KnotsCount=2 Degree=2 IsPeriodic=0
    g205: BSplineCurve PolesCount=2 KnotsCount=2 Degree=1 IsPeriodic=0
    g206: BSplineCurve PolesCount=3 KnotsCount=2 Degree=2 IsPeriodic=0
    g207: BSplineCurve PolesCount=3 KnotsCount=2 Degree=2 IsPeriodic=0
    g208: BSplineCurve PolesCount=2 KnotsCount=2 Degree=1 IsPeriodic=0
    g209: BSplineCurve PolesCount=2 KnotsCount=2 Degree=1 IsPeriodic=0
    g210: BSplineCurve PolesCount=2 KnotsCount=2 Degree=1 IsPeriodic=0
    g211: BSplineCurve PolesCount=2 KnotsCount=2 Degree=1 IsPeriodic=0
    g212: BSplineCurve PolesCount=2 KnotsCount=2 Degree=1 IsPeriodic=0
    g213: BSplineCurve PolesCount=2 KnotsCount=2 Degree=1 IsPeriodic=0
    g214: BSplineCurve PolesCount=2 KnotsCount=2 Degree=1 IsPeriodic=0
    g215: BSplineCurve PolesCount=2 KnotsCount=2 Degree=1 IsPeriodic=0
    g216: BSplineCurve PolesCount=2 KnotsCount=2 Degree=1 IsPeriodic=0
    g217: BSplineCurve PolesCount=2 KnotsCount=2 Degree=1 IsPeriodic=0
    g218: BSplineCurve PolesCount=2 KnotsCount=2 Degree=1 IsPeriodic=0
    g219: BSplineCurve PolesCount=2 KnotsCount=2 Degree=1 IsPeriodic=0
    g220: BSplineCurve PolesCount=2 KnotsCount=2 Degree=1 IsPeriodic=0
    g221: BSplineCurve PolesCount=2 KnotsCount=2 Degree=1 IsPeriodic=0
    g222: BSplineCurve PolesCount=2 KnotsCount=2 Degree=1 IsPeriodic=0
    g223: BSplineCurve PolesCount=2 KnotsCount=2 Degree=1 IsPeriodic=0
    g224: BSplineCurve PolesCount=3 KnotsCount=2 Degree=2 IsPeriodic=0
    g225: BSplineCurve PolesCount=3 KnotsCount=2 Degree=2 IsPeriodic=0
    g226: BSplineCurve PolesCount=3 KnotsCount=2 Degree=2 IsPeriodic=0
    g227: BSplineCurve PolesCount=3 KnotsCount=2 Degree=2 IsPeriodic=0
    g228: BSplineCurve PolesCount=3 KnotsCount=2 Degree=2 IsPeriodic=0
    g229: BSplineCurve PolesCount=3 KnotsCount=2 Degree=2 IsPeriodic=0
    g230: BSplineCurve PolesCount=2 KnotsCount=2 Degree=1 IsPeriodic=0
    g231: BSplineCurve PolesCount=3 KnotsCount=2 Degree=2 IsPeriodic=0
    g232: BSplineCurve PolesCount=3 KnotsCount=2 Degree=2 IsPeriodic=0
    g233: BSplineCurve PolesCount=3 KnotsCount=2 Degree=2 IsPeriodic=0
    g234: BSplineCurve PolesCount=3 KnotsCount=2 Degree=2 IsPeriodic=0
    g235: BSplineCurve PolesCount=3 KnotsCount=2 Degree=2 IsPeriodic=0
    g236: BSplineCurve PolesCount=3 KnotsCount=2 Degree=2 IsPeriodic=0
    g237: BSplineCurve PolesCount=3 KnotsCount=2 Degree=2 IsPeriodic=0
    g238: BSplineCurve PolesCount=2 KnotsCount=2 Degree=1 IsPeriodic=0
    g239: BSplineCurve PolesCount=2 KnotsCount=2 Degree=1 IsPeriodic=0
    g240: BSplineCurve PolesCount=2 KnotsCount=2 Degree=1 IsPeriodic=0
    g241: BSplineCurve PolesCount=2 KnotsCount=2 Degree=1 IsPeriodic=0
    g242: BSplineCurve PolesCount=2 KnotsCount=2 Degree=1 IsPeriodic=0
    g243: BSplineCurve PolesCount=2 KnotsCount=2 Degree=1 IsPeriodic=0
    g244: BSplineCurve PolesCount=3 KnotsCount=2 Degree=2 IsPeriodic=0
    g245: BSplineCurve PolesCount=3 KnotsCount=2 Degree=2 IsPeriodic=0
    g246: BSplineCurve PolesCount=3 KnotsCount=2 Degree=2 IsPeriodic=0
    g247: BSplineCurve PolesCount=3 KnotsCount=2 Degree=2 IsPeriodic=0
    g248: BSplineCurve PolesCount=3 KnotsCount=2 Degree=2 IsPeriodic=0
    g249: BSplineCurve PolesCount=3 KnotsCount=2 Degree=2 IsPeriodic=0
    g250: BSplineCurve PolesCount=3 KnotsCount=2 Degree=2 IsPeriodic=0
    g251: BSplineCurve PolesCount=3 KnotsCount=2 Degree=2 IsPeriodic=0
    g252: BSplineCurve PolesCount=3 KnotsCount=2 Degree=2 IsPeriodic=0
    g253: BSplineCurve PolesCount=3 KnotsCount=2 Degree=2 IsPeriodic=0
    g254: BSplineCurve PolesCount=3 KnotsCount=2 Degree=2 IsPeriodic=0
    g255: BSplineCurve PolesCount=3 KnotsCount=2 Degree=2 IsPeriodic=0
    g256: BSplineCurve PolesCount=3 KnotsCount=2 Degree=2 IsPeriodic=0
    g257: BSplineCurve PolesCount=3 KnotsCount=2 Degree=2 IsPeriodic=0
    g258: BSplineCurve PolesCount=3 KnotsCount=2 Degree=2 IsPeriodic=0
    g259: BSplineCurve PolesCount=3 KnotsCount=2 Degree=2 IsPeriodic=0
    g260: BSplineCurve PolesCount=3 KnotsCount=2 Degree=2 IsPeriodic=0
    g261: BSplineCurve PolesCount=2 KnotsCount=2 Degree=1 IsPeriodic=0
    g262: BSplineCurve PolesCount=3 KnotsCount=2 Degree=2 IsPeriodic=0
    g263: BSplineCurve PolesCount=3 KnotsCount=2 Degree=2 IsPeriodic=0
    g264: BSplineCurve PolesCount=3 KnotsCount=2 Degree=2 IsPeriodic=0
    g265: BSplineCurve PolesCount=3 KnotsCount=2 Degree=2 IsPeriodic=0
    g266: BSplineCurve PolesCount=3 KnotsCount=2 Degree=2 IsPeriodic=0
    g267: BSplineCurve PolesCount=3 KnotsCount=2 Degree=2 IsPeriodic=0
    g268: BSplineCurve PolesCount=3 KnotsCount=2 Degree=2 IsPeriodic=0
    g269: BSplineCurve PolesCount=3 KnotsCount=2 Degree=2 IsPeriodic=0
    g270: BSplineCurve PolesCount=3 KnotsCount=2 Degree=2 IsPeriodic=0
    g271: BSplineCurve PolesCount=3 KnotsCount=2 Degree=2 IsPeriodic=0
    g272: BSplineCurve PolesCount=3 KnotsCount=2 Degree=2 IsPeriodic=0
    g273: BSplineCurve PolesCount=2 KnotsCount=2 Degree=1 IsPeriodic=0
    g274: BSplineCurve PolesCount=3 KnotsCount=2 Degree=2 IsPeriodic=0
    g275: BSplineCurve PolesCount=3 KnotsCount=2 Degree=2 IsPeriodic=0
    g276: BSplineCurve PolesCount=2 KnotsCount=2 Degree=1 IsPeriodic=0
    g277: BSplineCurve PolesCount=2 KnotsCount=2 Degree=1 IsPeriodic=0
    g278: BSplineCurve PolesCount=2 KnotsCount=2 Degree=1 IsPeriodic=0
    g279: BSplineCurve PolesCount=2 KnotsCount=2 Degree=1 IsPeriodic=0
    g280: BSplineCurve PolesCount=3 KnotsCount=2 Degree=2 IsPeriodic=0
    g281: BSplineCurve PolesCount=3 KnotsCount=2 Degree=2 IsPeriodic=0
    g282: BSplineCurve PolesCount=3 KnotsCount=2 Degree=2 IsPeriodic=0
    g283: BSplineCurve PolesCount=3 KnotsCount=2 Degree=2 IsPeriodic=0
    g284: BSplineCurve PolesCount=3 KnotsCount=2 Degree=2 IsPeriodic=0
    g285: BSplineCurve PolesCount=2 KnotsCount=2 Degree=1 IsPeriodic=0
    g286: BSplineCurve PolesCount=3 KnotsCount=2 Degree=2 IsPeriodic=0
    g287: BSplineCurve PolesCount=3 KnotsCount=2 Degree=2 IsPeriodic=0
    g288: BSplineCurve PolesCount=3 KnotsCount=2 Degree=2 IsPeriodic=0
    g289: BSplineCurve PolesCount=3 KnotsCount=2 Degree=2 IsPeriodic=0
    g290: BSplineCurve PolesCount=3 KnotsCount=2 Degree=2 IsPeriodic=0
    g291: BSplineCurve PolesCount=3 KnotsCount=2 Degree=2 IsPeriodic=0
    g292: BSplineCurve PolesCount=2 KnotsCount=2 Degree=1 IsPeriodic=0
    g293: BSplineCurve PolesCount=3 KnotsCount=2 Degree=2 IsPeriodic=0
    g294: BSplineCurve PolesCount=3 KnotsCount=2 Degree=2 IsPeriodic=0
    g295: BSplineCurve PolesCount=3 KnotsCount=2 Degree=2 IsPeriodic=0
    g296: BSplineCurve PolesCount=3 KnotsCount=2 Degree=2 IsPeriodic=0
    g297: BSplineCurve PolesCount=3 KnotsCount=2 Degree=2 IsPeriodic=0
    g298: BSplineCurve PolesCount=3 KnotsCount=2 Degree=2 IsPeriodic=0
    g299: BSplineCurve PolesCount=3 KnotsCount=2 Degree=2 IsPeriodic=0
    g300: BSplineCurve PolesCount=3 KnotsCount=2 Degree=2 IsPeriodic=0
    g301: BSplineCurve PolesCount=3 KnotsCount=2 Degree=2 IsPeriodic=0
    g302: BSplineCurve PolesCount=3 KnotsCount=2 Degree=2 IsPeriodic=0
    g303: BSplineCurve PolesCount=3 KnotsCount=2 Degree=2 IsPeriodic=0
    g304: BSplineCurve PolesCount=3 KnotsCount=2 Degree=2 IsPeriodic=0
    g305: BSplineCurve PolesCount=3 KnotsCount=2 Degree=2 IsPeriodic=0
    g306: BSplineCurve PolesCount=3 KnotsCount=2 Degree=2 IsPeriodic=0
    g307: BSplineCurve PolesCount=3 KnotsCount=2 Degree=2 IsPeriodic=0
    g308: BSplineCurve PolesCount=3 KnotsCount=2 Degree=2 IsPeriodic=0
    g309: BSplineCurve PolesCount=3 KnotsCount=2 Degree=2 IsPeriodic=0
    g310: BSplineCurve PolesCount=3 KnotsCount=2 Degree=2 IsPeriodic=0
    g311: BSplineCurve PolesCount=3 KnotsCount=2 Degree=2 IsPeriodic=0
    g312: BSplineCurve PolesCount=3 KnotsCount=2 Degree=2 IsPeriodic=0
    g313: BSplineCurve PolesCount=3 KnotsCount=2 Degree=2 IsPeriodic=0
    g314: BSplineCurve PolesCount=3 KnotsCount=2 Degree=2 IsPeriodic=0
    g315: BSplineCurve PolesCount=3 KnotsCount=2 Degree=2 IsPeriodic=0
    g316: BSplineCurve PolesCount=3 KnotsCount=2 Degree=2 IsPeriodic=0
    g317: BSplineCurve PolesCount=3 KnotsCount=2 Degree=2 IsPeriodic=0
    g318: BSplineCurve PolesCount=3 KnotsCount=2 Degree=2 IsPeriodic=0
    g319: BSplineCurve PolesCount=3 KnotsCount=2 Degree=2 IsPeriodic=0
    g320: BSplineCurve PolesCount=2 KnotsCount=2 Degree=1 IsPeriodic=0
    g321: BSplineCurve PolesCount=3 KnotsCount=2 Degree=2 IsPeriodic=0
    g322: BSplineCurve PolesCount=3 KnotsCount=2 Degree=2 IsPeriodic=0
    g323: BSplineCurve PolesCount=3 KnotsCount=2 Degree=2 IsPeriodic=0
    g324: BSplineCurve PolesCount=3 KnotsCount=2 Degree=2 IsPeriodic=0
    g325: BSplineCurve PolesCount=3 KnotsCount=2 Degree=2 IsPeriodic=0
    g326: BSplineCurve PolesCount=3 KnotsCount=2 Degree=2 IsPeriodic=0
    g327: BSplineCurve PolesCount=3 KnotsCount=2 Degree=2 IsPeriodic=0
    g328: BSplineCurve PolesCount=3 KnotsCount=2 Degree=2 IsPeriodic=0
    g329: BSplineCurve PolesCount=3 KnotsCount=2 Degree=2 IsPeriodic=0
    g330: BSplineCurve PolesCount=3 KnotsCount=2 Degree=2 IsPeriodic=0
    g331: BSplineCurve PolesCount=3 KnotsCount=2 Degree=2 IsPeriodic=0
    g332: BSplineCurve PolesCount=3 KnotsCount=2 Degree=2 IsPeriodic=0
    g333: BSplineCurve PolesCount=3 KnotsCount=2 Degree=2 IsPeriodic=0
    g334: BSplineCurve PolesCount=3 KnotsCount=2 Degree=2 IsPeriodic=0
    g335: BSplineCurve PolesCount=3 KnotsCount=2 Degree=2 IsPeriodic=0
    g336: BSplineCurve PolesCount=3 KnotsCount=2 Degree=2 IsPeriodic=0
    g337: BSplineCurve PolesCount=2 KnotsCount=2 Degree=1 IsPeriodic=0
    g338: BSplineCurve PolesCount=2 KnotsCount=2 Degree=1 IsPeriodic=0
    g339: BSplineCurve PolesCount=2 KnotsCount=2 Degree=1 IsPeriodic=0
    g340: BSplineCurve PolesCount=2 KnotsCount=2 Degree=1 IsPeriodic=0
    g341: BSplineCurve PolesCount=2 KnotsCount=2 Degree=1 IsPeriodic=0
    g342: BSplineCurve PolesCount=2 KnotsCount=2 Degree=1 IsPeriodic=0
    g343: BSplineCurve PolesCount=2 KnotsCount=2 Degree=1 IsPeriodic=0
    g344: BSplineCurve PolesCount=2 KnotsCount=2 Degree=1 IsPeriodic=0
    g345: BSplineCurve PolesCount=2 KnotsCount=2 Degree=1 IsPeriodic=0
    g346: BSplineCurve PolesCount=2 KnotsCount=2 Degree=1 IsPeriodic=0
    g347: BSplineCurve PolesCount=2 KnotsCount=2 Degree=1 IsPeriodic=0
    g348: BSplineCurve PolesCount=3 KnotsCount=2 Degree=2 IsPeriodic=0
    g349: BSplineCurve PolesCount=3 KnotsCount=2 Degree=2 IsPeriodic=0
    g350: BSplineCurve PolesCount=3 KnotsCount=2 Degree=2 IsPeriodic=0
    g351: BSplineCurve PolesCount=3 KnotsCount=2 Degree=2 IsPeriodic=0
    g352: BSplineCurve PolesCount=3 KnotsCount=2 Degree=2 IsPeriodic=0
    g353: BSplineCurve PolesCount=3 KnotsCount=2 Degree=2 IsPeriodic=0
    g354: BSplineCurve PolesCount=3 KnotsCount=2 Degree=2 IsPeriodic=0
    g355: BSplineCurve PolesCount=3 KnotsCount=2 Degree=2 IsPeriodic=0
    g356: BSplineCurve PolesCount=3 KnotsCount=2 Degree=2 IsPeriodic=0
    g357: BSplineCurve PolesCount=3 KnotsCount=2 Degree=2 IsPeriodic=0
    g358: BSplineCurve PolesCount=3 KnotsCount=2 Degree=2 IsPeriodic=0
    g359: BSplineCurve PolesCount=3 KnotsCount=2 Degree=2 IsPeriodic=0
    g360: BSplineCurve PolesCount=3 KnotsCount=2 Degree=2 IsPeriodic=0
    g361: BSplineCurve PolesCount=3 KnotsCount=2 Degree=2 IsPeriodic=0
    g362: BSplineCurve PolesCount=3 KnotsCount=2 Degree=2 IsPeriodic=0
    g363: BSplineCurve PolesCount=3 KnotsCount=2 Degree=2 IsPeriodic=0
    g364: BSplineCurve PolesCount=2 KnotsCount=2 Degree=1 IsPeriodic=0
    g365: BSplineCurve PolesCount=2 KnotsCount=2 Degree=1 IsPeriodic=0
    g366: BSplineCurve PolesCount=2 KnotsCount=2 Degree=1 IsPeriodic=0
    g367: BSplineCurve PolesCount=2 KnotsCount=2 Degree=1 IsPeriodic=0
    g368: BSplineCurve PolesCount=2 KnotsCount=2 Degree=1 IsPeriodic=0
    g369: BSplineCurve PolesCount=2 KnotsCount=2 Degree=1 IsPeriodic=0
    g370: BSplineCurve PolesCount=2 KnotsCount=2 Degree=1 IsPeriodic=0
    g371: BSplineCurve PolesCount=2 KnotsCount=2 Degree=1 IsPeriodic=0
    g372: BSplineCurve PolesCount=2 KnotsCount=2 Degree=1 IsPeriodic=0
    g373: BSplineCurve PolesCount=2 KnotsCount=2 Degree=1 IsPeriodic=0
    g374: BSplineCurve PolesCount=2 KnotsCount=2 Degree=1 IsPeriodic=0
    g375: BSplineCurve PolesCount=2 KnotsCount=2 Degree=1 IsPeriodic=0
    g376: BSplineCurve PolesCount=2 KnotsCount=2 Degree=1 IsPeriodic=0
    g377: BSplineCurve PolesCount=2 KnotsCount=2 Degree=1 IsPeriodic=0
    g378: BSplineCurve PolesCount=2 KnotsCount=2 Degree=1 IsPeriodic=0
    g379: BSplineCurve PolesCount=2 KnotsCount=2 Degree=1 IsPeriodic=0
    g380: BSplineCurve PolesCount=2 KnotsCount=2 Degree=1 IsPeriodic=0
    g381: BSplineCurve PolesCount=2 KnotsCount=2 Degree=1 IsPeriodic=0
    g382: BSplineCurve PolesCount=2 KnotsCount=2 Degree=1 IsPeriodic=0
    g383: BSplineCurve PolesCount=2 KnotsCount=2 Degree=1 IsPeriodic=0
    g384: BSplineCurve PolesCount=2 KnotsCount=2 Degree=1 IsPeriodic=0
    g385: BSplineCurve PolesCount=2 KnotsCount=2 Degree=1 IsPeriodic=0
    g386: BSplineCurve PolesCount=2 KnotsCount=2 Degree=1 IsPeriodic=0
    g387: BSplineCurve PolesCount=2 KnotsCount=2 Degree=1 IsPeriodic=0
    g388: BSplineCurve PolesCount=2 KnotsCount=2 Degree=1 IsPeriodic=0
    g389: BSplineCurve PolesCount=2 KnotsCount=2 Degree=1 IsPeriodic=0
    g390: BSplineCurve PolesCount=2 KnotsCount=2 Degree=1 IsPeriodic=0
    g391: BSplineCurve PolesCount=2 KnotsCount=2 Degree=1 IsPeriodic=0
    g392: BSplineCurve PolesCount=2 KnotsCount=2 Degree=1 IsPeriodic=0
    g393: BSplineCurve PolesCount=2 KnotsCount=2 Degree=1 IsPeriodic=0
    g394: BSplineCurve PolesCount=2 KnotsCount=2 Degree=1 IsPeriodic=0
    g395: BSplineCurve PolesCount=2 KnotsCount=2 Degree=1 IsPeriodic=0
    g396: BSplineCurve PolesCount=2 KnotsCount=2 Degree=1 IsPeriodic=0
    g397: BSplineCurve PolesCount=2 KnotsCount=2 Degree=1 IsPeriodic=0
    g398: BSplineCurve PolesCount=3 KnotsCount=2 Degree=2 IsPeriodic=0
    g399: BSplineCurve PolesCount=3 KnotsCount=2 Degree=2 IsPeriodic=0
    ... +790 more geometry lines
  constraints (1190):
    c: Coincident(g93,g94)
    c: Coincident(g92,g93)
    c: Coincident(g282,g284)
    c: Coincident(g273,g274)
    c: Coincident(g272,g273)
    c: Coincident(g280,g282)
    c: Coincident(g88,g89)
    c: Coincident(g96,g97)
    c: Coincident(g299,g300)
    c: Coincident(g284,g286)
    c: Coincident(g298,g299)
    c: Coincident(g96,g99)
    c: Coincident(g89,g90)
    c: Coincident(g280,g281)
    c: Coincident(g271,g272)
    c: Coincident(g298,g304)
    c: Coincident(g300,g301)
    c: Coincident(g286,g288)
    c: Coincident(g274,g275)
    c: Coincident(g281,g283)
    c: Coincident(g303,g304)
    c: Coincident(g301,g302)
    c: Coincident(g288,g290)
    c: Coincident(g302,g303)
    c: Coincident(g283,g285)
    c: Coincident(g285,g287)
    c: Coincident(g290,g292)
    c: Coincident(g292,g294)
    c: Coincident(g270,g271)
    c: Coincident(g306,g308)
    c: Coincident(g287,g289)
    c: Coincident(g249,g251)
    c: Coincident(g314,g316)
    c: Coincident(g305,g306)
    c: Coincident(g308,g310)
    c: Coincident(g294,g296)
    c: Coincident(g251,g253)
    c: Coincident(g312,g314)
    c: Coincident(g263,g264)
    c: Coincident(g322,g324)
    c: Coincident(g316,g318)
    c: Coincident(g264,g265)
    c: Coincident(g289,g291)
    c: Coincident(g305,g307)
    c: Coincident(g324,g326)
    c: Coincident(g247,g249)
    c: Coincident(g310,g311)
    c: Coincident(g296,g297)
    c: Coincident(g262,g263)
    c: Coincident(g276,g277)
    c: Coincident(g320,g322)
    c: Coincident(g318,g320)
    c: Coincident(g265,g266)
    c: Coincident(g309,g311)
    c: Coincident(g275,g276)
    c: Coincident(g307,g309)
    c: Coincident(g291,g293)
    c: Coincident(g270,g279)
    c: Coincident(g325,g327)
    c: Coincident(g323,g325)
    c: Coincident(g100,g101)
    c: Coincident(g84,g85)
    c: Coincident(g253,g255)
    c: Coincident(g295,g297)
    c: Coincident(g277,g278)
    c: Coincident(g262,g269)
    c: Coincident(g312,g313)
    c: Coincident(g326,g327)
    c: Coincident(g247,g248)
    c: Coincident(g293,g295)
    c: Coincident(g329,g330)
    c: Coincident(g330,g331)
    c: Coincident(g278,g279)
    c: Coincident(g254,g256)
    c: Coincident(g266,g267)
    c: Coincident(g85,g86)
    c: Coincident(g100,g103)
    c: Coincident(g328,g329)
    c: Coincident(g321,g323)
    c: Coincident(g268,g269)
    c: Coincident(g267,g268)
    c: Coincident(g331,g332)
    c: Coincident(g94,g95)
    c: Coincident(g92,g95)
    c: Coincident(g252,g254)
    c: Coincident(g328,g336)
    c: Coincident(g248,g250)
    c: Coincident(g250,g252)
    c: Coincident(g332,g333)
    c: Coincident(g256,g258)
    c: Coincident(g319,g321)
    c: Coincident(g335,g336)
    c: Coincident(g255,g257)
    c: Coincident(g313,g315)
    c: Coincident(g88,g91)
    c: Coincident(g97,g98)
    c: Coincident(g260,g261)
    c: Coincident(g98,g99)
    c: Coincident(g90,g91)
    c: Coincident(g333,g334)
    c: Coincident(g259,g261)
    c: Coincident(g334,g335)
    c: Coincident(g258,g260)
    c: Coincident(g317,g319)
    c: Coincident(g348,g350)
    c: Coincident(g350,g352)
    c: Coincident(g315,g317)
    c: Coincident(g257,g259)
    c: Coincident(g357,g358)
    c: Coincident(g356,g357)
    c: Coincident(g228,g229)
    c: Coincident(g227,g228)
    c: Coincident(g346,g347)
    c: Coincident(g229,g230)
    c: Coincident(g352,g354)
    c: Coincident(g358,g359)
    c: Coincident(g231,g232)
    c: Coincident(g348,g349)
    c: Coincident(g230,g231)
    c: Coincident(g345,g346)
    c: Coincident(g356,g363)
    c: Coincident(g226,g227)
    c: Coincident(g232,g233)
    c: Coincident(g344,g345)
    c: Coincident(g238,g239)
    c: Coincident(g338,g339)
    c: Coincident(g237,g238)
    c: Coincident(g337,g347)
    c: Coincident(g359,g360)
    c: Coincident(g233,g234)
    c: Coincident(g236,g237)
    c: Coincident(g101,g102)
    c: Coincident(g84,g87)
    c: Coincident(g354,g355)
    c: Coincident(g243,g244)
    c: Coincident(g337,g338)
    c: Coincident(g362,g363)
    c: Coincident(g226,g246)
    c: Coincident(g349,g351)
    c: Coincident(g235,g236)
    c: Coincident(g234,g235)
    c: Coincident(g102,g103)
    c: Coincident(g86,g87)
    c: Coincident(g244,g245)
    c: Coincident(g80,g81)
    c: Coincident(g104,g105)
    c: Coincident(g245,g246)
    c: Coincident(g360,g361)
    c: Coincident(g361,g362)
    c: Coincident(g351,g353)
    c: Coincident(g242,g243)
    c: Coincident(g353,g355)
    c: Coincident(g239,g240)
    c: Coincident(g81,g82)
    c: Coincident(g104,g107)
    c: Coincident(g241,g242)
    c: Coincident(g340,g341)
    c: Coincident(g339,g340)
    c: Coincident(g240,g241)
    c: Coincident(g343,g344)
    c: Coincident(g341,g342)
    c: Coincident(g342,g343)
    c: Coincident(g384,g385)
    c: Coincident(g383,g384)
    c: Coincident(g382,g383)
    c: Coincident(g376,g377)
    c: Coincident(g214,g216)
    c: Coincident(g375,g385)
    c: Coincident(g373,g374)
    c: Coincident(g216,g218)
    c: Coincident(g80,g83)
    c: Coincident(g105,g106)
    c: Coincident(g375,g376)
    c: Coincident(g210,g212)
    c: Coincident(g220,g221)
    c: Coincident(g372,g373)
    c: Coincident(g221,g222)
    c: Coincident(g208,g210)
    c: Coincident(g222,g223)
    c: Coincident(g106,g107)
    c: Coincident(g82,g83)
    c: Coincident(g212,g214)
    c: Coincident(g371,g372)
    c: Coincident(g208,g209)
    c: Coincident(g219,g220)
    c: Coincident(g365,g366)
    c: Coincident(g213,g215)
    c: Coincident(g209,g211)
    c: Coincident(g364,g374)
    c: Coincident(g377,g378)
    c: Coincident(g211,g213)
    c: Coincident(g364,g365)
    c: Coincident(g381,g382)
    c: Coincident(g378,g379)
    c: Coincident(g380,g381)
    c: Coincident(g379,g380)
    c: Coincident(g223,g224)
    c: Coincident(g224,g225)
    c: Coincident(g219,g225)
    c: Coincident(g217,g218)
    c: Coincident(g108,g109)
    c: Coincident(g76,g77)
    c: Coincident(g215,g217)
    c: Coincident(g366,g367)
    c: Coincident(g370,g371)
    c: Coincident(g367,g368)
    c: Coincident(g369,g370)
    c: Coincident(g368,g369)
    c: Coincident(g108,g111)
    c: Coincident(g77,g78)
    c: Coincident(g419,g420)
    c: Coincident(g418,g419)
    c: Coincident(g109,g110)
    c: Coincident(g76,g79)
    c: Coincident(g78,g79)
    c: Coincident(g110,g111)
    c: Coincident(g181,g182)
    c: Coincident(g414,g415)
    c: Coincident(g413,g414)
    c: Coincident(g415,g416)
    c: Coincident(g182,g183)
    c: Coincident(g417,g418)
    c: Coincident(g412,g413)
    c: Coincident(g416,g417)
    c: Coincident(g397,g420)
    c: Coincident(g401,g402)
    c: Coincident(g402,g403)
    c: Coincident(g400,g401)
    c: Coincident(g180,g181)
    c: Coincident(g397,g398)
    c: Coincident(g183,g184)
    c: Coincident(g403,g404)
    c: Coincident(g399,g400)
    c: Coincident(g398,g399)
    c: Coincident(g395,g396)
    c: Coincident(g184,g185)
    c: Coincident(g411,g412)
    c: Coincident(g394,g395)
    c: Coincident(g404,g405)
    c: Coincident(g189,g190)
    c: Coincident(g185,g186)
    c: Coincident(g198,g199)
    c: Coincident(g179,g180)
    c: Coincident(g188,g189)
    c: Coincident(g405,g406)
    c: Coincident(g190,g191)
    c: Coincident(g407,g408)
    c: Coincident(g393,g394)
    c: Coincident(g197,g198)
    c: Coincident(g191,g192)
    c: Coincident(g410,g411)
    c: Coincident(g406,g407)
    c: Coincident(g186,g187)
    c: Coincident(g187,g188)
    c: Coincident(g205,g206)
    c: Coincident(g204,g205)
    c: Coincident(g387,g388)
    c: Coincident(g408,g409)
    c: Coincident(g199,g200)
    c: Coincident(g179,g207)
    c: Coincident(g196,g197)
    c: Coincident(g409,g410)
    c: Coincident(g192,g193)
    c: Coincident(g206,g207)
    c: Coincident(g386,g396)
    c: Coincident(g195,g196)
    c: Coincident(g203,g204)
    c: Coincident(g386,g387)
    c: Coincident(g193,g194)
    c: Coincident(g200,g201)
    c: Coincident(g194,g195)
    c: Coincident(g202,g203)
    c: Coincident(g201,g202)
    c: Coincident(g392,g393)
    c: Coincident(g388,g389)
    c: Coincident(g391,g392)
    c: Coincident(g389,g390)
    c: Coincident(g112,g113)
    c: Coincident(g72,g73)
    c: Coincident(g390,g391)
    c: Coincident(g73,g74)
    c: Coincident(g112,g115)
    c: Coincident(g72,g75)
    c: Coincident(g113,g114)
    c: Coincident(g432,g433)
    c: Coincident(g432,g460)
    c: Coincident(g74,g75)
    c: Coincident(g114,g115)
    c: Coincident(g438,g439)
    c: Coincident(g439,g440)
    c: Coincident(g459,g460)
    c: Coincident(g433,g434)
    c: Coincident(g437,g438)
    c: Coincident(g456,g457)
    c: Coincident(g440,g441)
    c: Coincident(g155,g178)
    c: Coincident(g455,g456)
    c: Coincident(g155,g156)
    c: Coincident(g458,g459)
    c: Coincident(g457,g458)
    c: Coincident(g445,g446)
    c: Coincident(g446,g447)
    c: Coincident(g434,g435)
    c: Coincident(g175,g176)
    c: Coincident(g454,g455)
    c: Coincident(g441,g442)
    c: Coincident(g156,g157)
    c: Coincident(g447,g448)
    c: Coincident(g444,g445)
    c: Coincident(g442,g443)
    c: Coincident(g436,g437)
    c: Coincident(g174,g175)
    c: Coincident(g443,g444)
    c: Coincident(g157,g158)
    c: Coincident(g430,g431)
    c: Coincident(g166,g167)
    c: Coincident(g435,g436)
    c: Coincident(g448,g449)
    c: Coincident(g429,g430)
    c: Coincident(g453,g454)
    c: Coincident(g173,g174)
    c: Coincident(g450,g451)
    c: Coincident(g449,g450)
    c: Coincident(g165,g166)
    c: Coincident(g158,g159)
    c: Coincident(g167,g168)
    c: Coincident(g164,g165)
    c: Coincident(g451,g452)
    c: Coincident(g452,g453)
    c: Coincident(g177,g178)
    c: Coincident(g159,g160)
    c: Coincident(g428,g429)
    c: Coincident(g176,g177)
    c: Coincident(g172,g173)
    c: Coincident(g163,g164)
    c: Coincident(g160,g161)
    c: Coincident(g422,g423)
    c: Coincident(g168,g169)
    c: Coincident(g161,g162)
    c: Coincident(g162,g163)
    c: Coincident(g171,g172)
    c: Coincident(g421,g431)
    c: Coincident(g170,g171)
    c: Coincident(g169,g170)
    c: Coincident(g421,g422)
    c: Coincident(g427,g428)
    c: Coincident(g423,g424)
    c: Coincident(g426,g427)
    c: Coincident(g424,g425)
    c: Coincident(g425,g426)
    c: Coincident(g68,g69)
    c: Coincident(g116,g117)
    c: Coincident(g116,g119)
    c: Coincident(g69,g70)
    c: Coincident(g68,g71)
    c: Coincident(g117,g118)
    c: Coincident(g118,g119)
    c: Coincident(g70,g71)
    c: Coincident(g473,g475)
    c: Coincident(g475,g477)
    c: Coincident(g472,g474)
    c: Coincident(g472,g473)
    c: Coincident(g477,g479)
    c: Coincident(g474,g476)
    c: Coincident(g476,g478)
    c: Coincident(g483,g484)
    c: Coincident(g479,g481)
    c: Coincident(g144,g154)
    c: Coincident(g144,g145)
    c: Coincident(g483,g489)
    c: Coincident(g488,g489)
    c: Coincident(g487,g488)
    c: Coincident(g481,g482)
    c: Coincident(g486,g487)
    c: Coincident(g485,g486)
    c: Coincident(g484,g485)
    c: Coincident(g147,g148)
    c: Coincident(g148,g149)
    c: Coincident(g145,g146)
    c: Coincident(g478,g480)
    c: Coincident(g480,g482)
    c: Coincident(g470,g471)
    c: Coincident(g469,g470)
    c: Coincident(g151,g152)
    c: Coincident(g146,g147)
    c: Coincident(g149,g150)
    c: Coincident(g153,g154)
    c: Coincident(g468,g469)
    c: Coincident(g152,g153)
    c: Coincident(g150,g151)
    c: Coincident(g462,g463)
    c: Coincident(g467,g468)
    c: Coincident(g461,g471)
    c: Coincident(g463,g464)
    c: Coincident(g461,g462)
    c: Coincident(g466,g467)
    c: Coincident(g464,g465)
    c: Coincident(g465,g466)
    c: Coincident(g64,g65)
    c: Coincident(g120,g121)
    c: Coincident(g121,g122)
    c: Coincident(g64,g67)
    c: Coincident(g120,g123)
    c: Coincident(g65,g66)
    c: Coincident(g122,g123)
    c: Coincident(g66,g67)
    c: Coincident(g501,g521)
    c: Coincident(g501,g502)
    c: Coincident(g520,g521)
    c: Coincident(g516,g517)
    c: Coincident(g515,g516)
    c: Coincident(g508,g509)
    c: Coincident(g507,g508)
    c: Coincident(g509,g510)
    c: Coincident(g502,g503)
    c: Coincident(g506,g507)
    c: Coincident(g519,g520)
    c: Coincident(g510,g511)
    c: Coincident(g134,g135)
    c: Coincident(g511,g512)
    c: Coincident(g132,g134)
    c: Coincident(g133,g135)
    c: Coincident(g139,g140)
    c: Coincident(g512,g513)
    c: Coincident(g505,g506)
    c: Coincident(g503,g504)
    c: Coincident(g518,g519)
    c: Coincident(g517,g518)
    c: Coincident(g138,g139)
    c: Coincident(g140,g141)
    c: Coincident(g513,g514)
    c: Coincident(g504,g505)
    c: Coincident(g514,g515)
    c: Coincident(g130,g132)
    c: Coincident(g137,g138)
    c: Coincident(g499,g500)
    c: Coincident(g498,g499)
    c: Coincident(g141,g142)
    c: Coincident(g131,g133)
    c: Coincident(g136,g137)
    c: Coincident(g142,g143)
    c: Coincident(g136,g143)
    c: Coincident(g128,g130)
    c: Coincident(g497,g498)
    c: Coincident(g129,g131)
    c: Coincident(g128,g129)
    c: Coincident(g496,g497)
    c: Coincident(g491,g492)
    c: Coincident(g492,g493)
    c: Coincident(g495,g496)
    c: Coincident(g490,g500)
    c: Coincident(g490,g491)
    c: Coincident(g493,g494)
    c: Coincident(g494,g495)
    c: Coincident(g124,g125)
    c: Coincident(g125,g126)
    c: Coincident(g60,g61)
    c: Coincident(g61,g62)
    c: Coincident(g60,g63)
    c: Coincident(g62,g63)
    c: Coincident(g124,g127)
    c: Coincident(g126,g127)
    c: Coincident(g1169,g1170)
    c: Coincident(g545,g547)
    c: Coincident(g1153,g1154)
    c: Coincident(g533,g534)
    c: Coincident(g1170,g1171)
    c: Coincident(g534,g536)
    c: Coincident(g1168,g1169)
    c: Coincident(g546,g547)
    c: Coincident(g533,g535)
    c: Coincident(g1152,g1153)
    c: Coincident(g548,g555)
    c: Coincident(g1154,g1155)
    c: Coincident(g1167,g1168)
    c: Coincident(g554,g555)
    c: Coincident(g548,g549)
    c: Coincident(g1161,g1162)
    c: Coincident(g1160,g1161)
    c: Coincident(g543,g545)
    c: Coincident(g544,g546)
    c: Coincident(g1171,g1172)
    c: Coincident(g536,g538)
    c: Coincident(g1166,g1167)
    c: Coincident(g1162,g1163)
    c: Coincident(g1159,g1160)
    c: Coincident(g553,g554)
    c: Coincident(g549,g550)
    c: Coincident(g535,g537)
    c: Coincident(g1155,g1156)
    c: Coincident(g1151,g1152)
    c: Coincident(g538,g540)
    c: Coincident(g1165,g1166)
    c: Coincident(g1175,g1176)
    c: Coincident(g1176,g1177)
    c: Coincident(g542,g544)
    c: Coincident(g1163,g1164)
    c: Coincident(g552,g553)
    c: Coincident(g1158,g1159)
    c: Coincident(g1164,g1165)
    c: Coincident(g550,g551)
    c: Coincident(g1172,g1173)
    c: Coincident(g1156,g1157)
    c: Coincident(g541,g543)
    c: Coincident(g540,g542)
    c: Coincident(g551,g552)
    c: Coincident(g1157,g1158)
    c: Coincident(g1174,g1175)
    c: Coincident(g537,g539)
    c: Coincident(g1177,g1178)
    c: Coincident(g1173,g1174)
    c: Coincident(g1150,g1151)
    c: Coincident(g539,g541)
    c: Coincident(g1150,g1178)
    c: Coincident(g1183,g1184)
    c: Coincident(g530,g531)
    c: Coincident(g1182,g1183)
    c: Coincident(g531,g532)
    c: Coincident(g1179,g1180)
    c: Coincident(g1179,g1189)
    c: Coincident(g528,g529)
    c: Coincident(g1184,g1185)
    c: Coincident(g1181,g1182)
    c: Coincident(g529,g530)
    c: Coincident(g527,g528)
    c: Coincident(g1180,g1181)
    c: Coincident(g524,g525)
    c: Coincident(g1185,g1186)
    c: Coincident(g523,g524)
    c: Coincident(g1186,g1187)
    c: Coincident(g526,g527)
    c: Coincident(g525,g526)
    c: Coincident(g522,g523)
    c: Coincident(g522,g532)
    c: Coincident(g1187,g1188)
    c: Coincident(g1188,g1189)
    c: Coincident(g56,g57)
    c: Coincident(g0,g1)
    c: Coincident(g0,g3)
    c: Coincident(g57,g58)
    c: Coincident(g1,g2)
    c: Coincident(g56,g59)
    c: Coincident(g2,g3)
    c: Coincident(g58,g59)
    c: Coincident(g575,g576)
    c: Coincident(g567,g576)
    c: Coincident(g1124,g1125)
    c: Coincident(g1125,g1126)
    c: Coincident(g572,g573)
    c: Coincident(g1123,g1124)
    c: Coincident(g1108,g1109)
    c: Coincident(g1122,g1123)
    c: Coincident(g1126,g1127)
    c: Coincident(g1109,g1110)
    c: Coincident(g1121,g1122)
    c: Coincident(g1116,g1117)
    c: Coincident(g567,g568)
    c: Coincident(g1107,g1108)
    c: Coincident(g1115,g1116)
    c: Coincident(g1117,g1118)
    c: Coincident(g1114,g1115)
    c: Coincident(g1120,g1121)
    c: Coincident(g568,g569)
    c: Coincident(g1118,g1119)
    c: Coincident(g571,g572)
    c: Coincident(g1127,g1128)
    c: Coincident(g1130,g1131)
    c: Coincident(g1131,g1132)
    c: Coincident(g1119,g1120)
    c: Coincident(g1110,g1111)
    c: Coincident(g1106,g1107)
    c: Coincident(g569,g570)
    c: Coincident(g1113,g1114)
    c: Coincident(g574,g575)
    c: Coincident(g573,g574)
    c: Coincident(g1129,g1130)
    c: Coincident(g1128,g1129)
    c: Coincident(g1111,g1112)
    c: Coincident(g1112,g1113)
    c: Coincident(g570,g571)
    c: Coincident(g1132,g1133)
    c: Coincident(g1105,g1106)
    c: Coincident(g1105,g1133)
    c: Coincident(g1139,g1141)
    c: Coincident(g1140,g1141)
    c: Coincident(g1146,g1147)
    c: Coincident(g562,g563)
    c: Coincident(g1145,g1146)
    c: Coincident(g564,g565)
    c: Coincident(g565,g566)
    c: Coincident(g1137,g1139)
    c: Coincident(g1138,g1140)
    c: Coincident(g561,g562)
    c: Coincident(g1147,g1148)
    c: Coincident(g558,g559)
    c: Coincident(g1144,g1145)
    c: Coincident(g563,g564)
    c: Coincident(g1148,g1149)
    c: Coincident(g1143,g1144)
    c: Coincident(g1135,g1137)
    c: Coincident(g1136,g1138)
    c: Coincident(g557,g558)
    c: Coincident(g560,g561)
    c: Coincident(g559,g560)
    c: Coincident(g1142,g1149)
    c: Coincident(g1142,g1143)
    c: Coincident(g1134,g1135)
    c: Coincident(g1134,g1136)
    c: Coincident(g556,g557)
    c: Coincident(g556,g566)
    c: Coincident(g4,g5)
    c: Coincident(g52,g53)
    c: Coincident(g5,g6)
    c: Coincident(g52,g55)
    c: Coincident(g53,g54)
    c: Coincident(g4,g7)
    c: Coincident(g54,g55)
    c: Coincident(g6,g7)
    c: Coincident(g599,g601)
    c: Coincident(g1068,g1069)
    c: Coincident(g1067,g1068)
    c: Coincident(g597,g599)
    c: Coincident(g1065,g1066)
    c: Coincident(g595,g597)
    c: Coincident(g1066,g1067)
    c: Coincident(g613,g615)
    c: Coincident(g601,g603)
    c: Coincident(g1069,g1070)
    c: Coincident(g589,g591)
    c: Coincident(g588,g589)
    c: Coincident(g615,g617)
    c: Coincident(g1064,g1065)
    c: Coincident(g613,g614)
    c: Coincident(g593,g595)
    c: Coincident(g591,g593)
    c: Coincident(g611,g612)
    c: Coincident(g1056,g1057)
    c: Coincident(g1057,g1058)
    c: Coincident(g606,g612)
    c: Coincident(g1056,g1079)
    c: Coincident(g617,g619)
    c: Coincident(g1063,g1064)
    c: Coincident(g1058,g1059)
    c: Coincident(g614,g616)
    c: Coincident(g588,g590)
    c: Coincident(g603,g605)
    c: Coincident(g1070,g1071)
    c: Coincident(g1059,g1060)
    c: Coincident(g610,g611)
    c: Coincident(g1076,g1077)
    c: Coincident(g1075,g1076)
    c: Coincident(g606,g607)
    c: Coincident(g618,g619)
    c: Coincident(g1062,g1063)
    c: Coincident(g1060,g1061)
    c: Coincident(g616,g618)
    c: Coincident(g1061,g1062)
    c: Coincident(g1074,g1075)
    c: Coincident(g600,g602)
    c: Coincident(g598,g600)
    c: Coincident(g604,g605)
    c: Coincident(g1071,g1072)
    c: Coincident(g609,g610)
    c: Coincident(g1073,g1074)
    c: Coincident(g602,g604)
    c: Coincident(g607,g608)
    c: Coincident(g1072,g1073)
    c: Coincident(g590,g592)
    c: Coincident(g596,g598)
    c: Coincident(g608,g609)
    c: Coincident(g1085,g1087)
    c: Coincident(g1087,g1089)
    c: Coincident(g583,g584)
    c: Coincident(g594,g596)
    c: Coincident(g1101,g1102)
    c: Coincident(g592,g594)
    c: Coincident(g1100,g1101)
    c: Coincident(g1083,g1085)
    c: Coincident(g1077,g1078)
    c: Coincident(g582,g583)
    c: Coincident(g1102,g1103)
    c: Coincident(g1089,g1091)
    c: Coincident(g1078,g1079)
    c: Coincident(g579,g580)
    c: Coincident(g1099,g1100)
    c: Coincident(g1086,g1088)
    c: Coincident(g585,g586)
    c: Coincident(g586,g587)
    c: Coincident(g1088,g1090)
    c: Coincident(g1103,g1104)
    c: Coincident(g1098,g1099)
    c: Coincident(g1084,g1086)
    c: Coincident(g1081,g1083)
    c: Coincident(g1091,g1093)
    c: Coincident(g581,g582)
    c: Coincident(g1097,g1098)
    c: Coincident(g584,g585)
    c: Coincident(g1096,g1104)
    c: Coincident(g580,g581)
    c: Coincident(g1096,g1097)
    c: Coincident(g1093,g1095)
    c: Coincident(g1090,g1092)
    c: Coincident(g1094,g1095)
    c: Coincident(g578,g579)
    c: Coincident(g1082,g1084)
    c: Coincident(g1092,g1094)
    c: Coincident(g1080,g1081)
    c: Coincident(g48,g49)
    c: Coincident(g8,g9)
    c: Coincident(g1080,g1082)
    c: Coincident(g577,g578)
    c: Coincident(g577,g587)
    c: Coincident(g9,g10)
    c: Coincident(g48,g51)
    c: Coincident(g8,g11)
    c: Coincident(g49,g50)
    c: Coincident(g1012,g1013)
    c: Coincident(g632,g634)
    c: Coincident(g50,g51)
    c: Coincident(g10,g11)
    c: Coincident(g1011,g1012)
    c: Coincident(g1009,g1010)
    c: Coincident(g1013,g1014)
    c: Coincident(g634,g636)
    c: Coincident(g654,g655)
    c: Coincident(g1010,g1011)
    c: Coincident(g631,g632)
    c: Coincident(g1008,g1009)
    c: Coincident(g653,g654)
    c: Coincident(g647,g655)
    c: Coincident(g647,g648)
    c: Coincident(g645,g646)
    c: Coincident(g1007,g1008)
    c: Coincident(g652,g653)
    c: Coincident(g1014,g1015)
    c: Coincident(g636,g638)
    c: Coincident(g648,g649)
    c: Coincident(g1001,g1002)
    c: Coincident(g644,g646)
    c: Coincident(g1002,g1003)
    c: Coincident(g1006,g1007)
    c: Coincident(g1000,g1001)
    c: Coincident(g1003,g1004)
    c: Coincident(g1005,g1006)
    c: Coincident(g1004,g1005)
    c: Coincident(g649,g650)
    c: Coincident(g651,g652)
    c: Coincident(g631,g633)
    c: Coincident(g1000,g1023)
    c: Coincident(g643,g645)
    c: Coincident(g1019,g1020)
    c: Coincident(g1015,g1016)
    c: Coincident(g1020,g1021)
    c: Coincident(g1018,g1019)
    c: Coincident(g650,g651)
    c: Coincident(g642,g644)
    c: Coincident(g1016,g1017)
    c: Coincident(g638,g640)
    c: Coincident(g1017,g1018)
    c: Coincident(g1039,g1041)
    c: Coincident(g1040,g1041)
    c: Coincident(g626,g627)
    c: Coincident(g640,g642)
    c: Coincident(g1053,g1055)
    c: Coincident(g641,g643)
    c: Coincident(g1037,g1039)
    c: Coincident(g1054,g1055)
    c: Coincident(g625,g626)
    c: Coincident(g639,g641)
    c: Coincident(g633,g635)
    c: Coincident(g1038,g1040)
    c: Coincident(g1051,g1053)
    c: Coincident(g622,g623)
    c: Coincident(g637,g639)
    c: Coincident(g1032,g1034)
    c: Coincident(g1052,g1054)
    c: Coincident(g635,g637)
    c: Coincident(g1036,g1038)
    c: Coincident(g1034,g1036)
    c: Coincident(g1030,g1032)
    c: Coincident(g1021,g1022)
    c: Coincident(g1035,g1037)
    c: Coincident(g1045,g1046)
    c: Coincident(g1022,g1023)
    c: Coincident(g1050,g1052)
    c: Coincident(g1044,g1045)
    c: Coincident(g1049,g1051)
    c: Coincident(g624,g625)
    c: Coincident(g628,g629)
    c: Coincident(g1046,g1047)
    c: Coincident(g1049,g1050)
    c: Coincident(g629,g630)
    c: Coincident(g623,g624)
    c: Coincident(g1033,g1035)
    c: Coincident(g1028,g1030)
    c: Coincident(g1029,g1031)
    c: Coincident(g1027,g1029)
    c: Coincident(g1031,g1033)
    c: Coincident(g1047,g1048)
    c: Coincident(g12,g13)
    c: Coincident(g44,g45)
    c: Coincident(g627,g628)
    c: Coincident(g1025,g1027)
    c: Coincident(g1043,g1044)
    c: Coincident(g621,g622)
    c: Coincident(g1042,g1048)
    c: Coincident(g1026,g1028)
    c: Coincident(g1042,g1043)
    c: Coincident(g44,g47)
    c: Coincident(g13,g14)
    c: Coincident(g1024,g1025)
    c: Coincident(g1024,g1026)
    c: Coincident(g620,g621)
    c: Coincident(g620,g630)
    c: Coincident(g978,g979)
    c: Coincident(g681,g683)
    c: Coincident(g45,g46)
    c: Coincident(g12,g15)
    c: Coincident(g977,g978)
    c: Coincident(g683,g685)
    c: Coincident(g979,g980)
    c: Coincident(g975,g976)
    c: Coincident(g694,g695)
    c: Coincident(g693,g694)
    c: Coincident(g974,g975)
    c: Coincident(g976,g977)
    c: Coincident(g680,g681)
    c: Coincident(g14,g15)
    c: Coincident(g46,g47)
    c: Coincident(g973,g974)
    c: Coincident(g980,g981)
    c: Coincident(g688,g695)
    c: Coincident(g692,g693)
    c: Coincident(g685,g687)
    c: Coincident(g997,g998)
    c: Coincident(g972,g973)
    c: Coincident(g971,g972)
    c: Coincident(g996,g997)
    c: Coincident(g981,g982)
    c: Coincident(g670,g671)
    c: Coincident(g970,g971)
    c: Coincident(g969,g970)
    c: Coincident(g968,g969)
    c: Coincident(g967,g968)
    c: Coincident(g982,g983)
    c: Coincident(g966,g967)
    c: Coincident(g669,g670)
    c: Coincident(g983,g984)
    c: Coincident(g671,g672)
    c: Coincident(g680,g682)
    c: Coincident(g688,g689)
    c: Coincident(g984,g985)
    c: Coincident(g691,g692)
    c: Coincident(g663,g664)
    c: Coincident(g985,g986)
    c: Coincident(g966,g989)
    c: Coincident(g986,g987)
    c: Coincident(g664,g665)
    c: Coincident(g662,g663)
    c: Coincident(g686,g687)
    c: Coincident(g672,g673)
    c: Coincident(g668,g669)
    c: Coincident(g665,g666)
    c: Coincident(g661,g662)
    c: Coincident(g689,g690)
    c: Coincident(g998,g999)
    c: Coincident(g995,g996)
    c: Coincident(g690,g691)
    c: Coincident(g673,g674)
    c: Coincident(g682,g684)
    c: Coincident(g990,g999)
    c: Coincident(g660,g661)
    c: Coincident(g40,g41)
    c: Coincident(g16,g17)
    c: Coincident(g666,g667)
    c: Coincident(g684,g686)
    c: Coincident(g987,g988)
    c: Coincident(g667,g668)
    c: Coincident(g994,g995)
    c: Coincident(g990,g991)
    c: Coincident(g659,g660)
    c: Coincident(g988,g989)
    c: Coincident(g677,g678)
    c: Coincident(g17,g18)
    c: Coincident(g40,g43)
    c: Coincident(g674,g675)
    c: Coincident(g678,g679)
    c: Coincident(g991,g992)
    c: Coincident(g658,g659)
    c: Coincident(g993,g994)
    c: Coincident(g675,g676)
    c: Coincident(g657,g658)
    c: Coincident(g992,g993)
    c: Coincident(g676,g677)
    c: Coincident(g656,g657)
    c: Coincident(g656,g679)
    c: Coincident(g931,g932)
    c: Coincident(g726,g727)
    c: Coincident(g932,g933)
    c: Coincident(g725,g726)
    c: Coincident(g928,g929)
    c: Coincident(g930,g931)
    c: Coincident(g927,g928)
    c: Coincident(g722,g723)
    c: Coincident(g929,g930)
    c: Coincident(g933,g934)
    c: Coincident(g926,g927)
    c: Coincident(g724,g725)
    c: Coincident(g41,g42)
    c: Coincident(g16,g19)
    c: Coincident(g925,g926)
    c: Coincident(g710,g711)
    c: Coincident(g709,g710)
    c: Coincident(g723,g724)
    c: Coincident(g934,g935)
    c: Coincident(g951,g953)
    c: Coincident(g953,g955)
    c: Coincident(g924,g925)
    c: Coincident(g703,g704)
    c: Coincident(g923,g924)
    c: Coincident(g42,g43)
    c: Coincident(g18,g19)
    c: Coincident(g704,g705)
    c: Coincident(g711,g712)
    c: Coincident(g935,g936)
    c: Coincident(g954,g956)
    c: Coincident(g922,g923)
    c: Coincident(g952,g954)
    c: Coincident(g921,g922)
    c: Coincident(g702,g703)
    c: Coincident(g936,g937)
    c: Coincident(g36,g37)
    c: Coincident(g20,g21)
    c: Coincident(g708,g709)
    c: Coincident(g920,g921)
    c: Coincident(g705,g706)
    c: Coincident(g712,g713)
    c: Coincident(g937,g938)
    c: Coincident(g728,g729)
    c: Coincident(g701,g702)
    c: Coincident(g938,g939)
    c: Coincident(g36,g39)
    c: Coincident(g21,g22)
    c: Coincident(g919,g920)
    c: Coincident(g956,g957)
    c: Coincident(g948,g950)
    c: Coincident(g949,g951)
    c: Coincident(g955,g957)
    c: Coincident(g939,g940)
    c: Coincident(g706,g707)
    c: Coincident(g946,g948)
    c: Coincident(g950,g952)
    c: Coincident(g713,g714)
    c: Coincident(g729,g730)
    c: Coincident(g919,g942)
    c: Coincident(g727,g728)
    c: Coincident(g700,g701)
    c: Coincident(g707,g708)
    c: Coincident(g962,g963)
    c: Coincident(g963,g964)
    c: Coincident(g721,g722)
    c: Coincident(g961,g962)
    c: Coincident(g699,g700)
    c: Coincident(g944,g946)
    c: Coincident(g964,g965)
    c: Coincident(g720,g721)
    c: Coincident(g940,g941)
    c: Coincident(g714,g715)
    c: Coincident(g717,g718)
    c: Coincident(g698,g699)
    c: Coincident(g720,g730)
    c: Coincident(g941,g942)
    c: Coincident(g947,g949)
    c: Coincident(g960,g961)
    c: Coincident(g958,g965)
    c: Coincident(g718,g719)
    c: Coincident(g715,g716)
    c: Coincident(g943,g944)
    c: Coincident(g768,g769)
    c: Coincident(g769,g770)
    c: Coincident(g887,g888)
    c: Coincident(g886,g887)
    c: Coincident(g697,g698)
    c: Coincident(g959,g960)
    c: Coincident(g958,g959)
    c: Coincident(g763,g764)
    c: Coincident(g716,g717)
    c: Coincident(g882,g883)
    c: Coincident(g762,g763)
    c: Coincident(g883,g884)
    c: Coincident(g945,g947)
    c: Coincident(g767,g768)
    c: Coincident(g888,g889)
    c: Coincident(g885,g886)
    c: Coincident(g943,g945)
    c: Coincident(g911,g912)
    c: Coincident(g770,g771)
    c: Coincident(g764,g765)
    c: Coincident(g696,g697)
    c: Coincident(g881,g882)
    c: Coincident(g884,g885)
    c: Coincident(g761,g762)
    c: Coincident(g24,g25)
    c: Coincident(g32,g33)
    c: Coincident(g744,g745)
    c: Coincident(g745,g746)
    c: Coincident(g696,g719)
    c: Coincident(g25,g26)
    c: Coincident(g32,g35)
    c: Coincident(g771,g772)
    c: Coincident(g914,g915)
    c: Coincident(g765,g766)
    c: Coincident(g880,g881)
    c: Coincident(g760,g761)
    c: Coincident(g912,g913)
    c: Coincident(g739,g740)
    c: Coincident(g738,g739)
    c: Coincident(g766,g767)
    c: Coincident(g889,g890)
    c: Coincident(g743,g744)
    c: Coincident(g746,g747)
    c: Coincident(g879,g880)
    c: Coincident(g740,g741)
    c: Coincident(g772,g773)
    c: Coincident(g759,g760)
    c: Coincident(g913,g914)
    c: Coincident(g737,g738)
    c: Coincident(g890,g891)
    c: Coincident(g878,g879)
    c: Coincident(g747,g748)
    c: Coincident(g28,g29)
    c: Coincident(g29,g30)
    c: Coincident(g877,g878)
    c: Coincident(g891,g892)
    c: Coincident(g758,g759)
    c: Coincident(g741,g742)
    c: Coincident(g736,g737)
    c: Coincident(g742,g743)
    c: Coincident(g876,g877)
    c: Coincident(g916,g917)
    c: Coincident(g915,g916)
    c: Coincident(g37,g38)
    c: Coincident(g20,g23)
    c: Coincident(g845,g846)
    c: Coincident(g824,g825)
    c: Coincident(g773,g774)
    c: Coincident(g892,g893)
    c: Coincident(g748,g749)
    c: Coincident(g735,g736)
    c: Coincident(g910,g911)
    c: Coincident(g757,g758)
    c: Coincident(g875,g876)
    c: Coincident(g908,g909)
    c: Coincident(g825,g826)
    c: Coincident(g844,g845)
    c: Coincident(g907,g908)
    c: Coincident(g909,g910)
    c: Coincident(g792,g793)
    c: Coincident(g22,g23)
    c: Coincident(g38,g39)
    c: Coincident(g823,g824)
    c: Coincident(g846,g847)
    c: Coincident(g893,g894)
    c: Coincident(g865,g866)
    c: Coincident(g840,g841)
    c: Coincident(g819,g820)
    c: Coincident(g863,g865)
    c: Coincident(g917,g918)
    c: Coincident(g793,g794)
    c: Coincident(g776,g777)
    c: Coincident(g841,g842)
    c: Coincident(g818,g819)
    c: Coincident(g734,g735)
    c: Coincident(g874,g875)
    c: Coincident(g906,g907)
    c: Coincident(g820,g821)
    c: Coincident(g839,g840)
    c: Coincident(g774,g775)
    c: Coincident(g791,g792)
    c: Coincident(g894,g895)
    c: Coincident(g756,g757)
    c: Coincident(g787,g788)
    c: Coincident(g786,g787)
    c: Coincident(g843,g844)
    c: Coincident(g826,g827)
    c: Coincident(g777,g778)
    c: Coincident(g874,g897)
    c: Coincident(g788,g789)
    c: Coincident(g867,g873)
    c: Coincident(g749,g750)
    c: Coincident(g842,g843)
    c: Coincident(g901,g902)
    c: Coincident(g817,g818)
    c: Coincident(g733,g734)
    c: Coincident(g902,g903)
    c: Coincident(g872,g873)
    c: Coincident(g775,g776)
    c: Coincident(g821,g822)
    c: Coincident(g822,g823)
    c: Coincident(g838,g839)
    c: Coincident(g847,g848)
    c: Coincident(g794,g795)
    c: Coincident(g905,g906)
    c: Coincident(g871,g872)
    c: Coincident(g895,g896)
    c: Coincident(g785,g786)
    c: Coincident(g755,g756)
    c: Coincident(g898,g918)
    c: Coincident(g752,g753)
    c: Coincident(g789,g790)
    c: Coincident(g790,g791)
    c: Coincident(g816,g817)
    c: Coincident(g827,g828)
    c: Coincident(g837,g838)
    c: Coincident(g750,g751)
    c: Coincident(g732,g733)
    c: Coincident(g848,g849)
    c: Coincident(g755,g778)
    c: Coincident(g896,g897)
    c: Coincident(g795,g796)
    c: Coincident(g784,g785)
    c: Coincident(g815,g816)
    c: Coincident(g900,g901)
    c: Coincident(g814,g815)
    c: Coincident(g904,g905)
    c: Coincident(g753,g754)
    c: Coincident(g903,g904)
    c: Coincident(g836,g837)
    c: Coincident(g828,g829)
    c: Coincident(g829,g830)
    c: Coincident(g751,g752)
    c: Coincident(g849,g850)
    c: Coincident(g783,g784)
    c: Coincident(g830,g831)
    c: Coincident(g796,g797)
    c: Coincident(g812,g813)
    c: Coincident(g835,g836)
    c: Coincident(g898,g899)
    c: Coincident(g813,g814)
    c: Coincident(g731,g732)
    c: Coincident(g899,g900)
    c: Coincident(g811,g812)
    c: Coincident(g782,g783)
    c: Coincident(g834,g835)
    c: Coincident(g731,g754)
    c: Coincident(g870,g871)
    c: Coincident(g850,g851)
    c: Coincident(g803,g831)
    c: Coincident(g810,g811)
    c: Coincident(g869,g870)
    c: Coincident(g864,g866)
    c: Coincident(g868,g869)
    c: Coincident(g833,g834)
    c: Coincident(g781,g782)
    c: Coincident(g797,g798)
    c: Coincident(g807,g808)
    c: Coincident(g867,g868)
    c: Coincident(g861,g863)
    c: Coincident(g851,g852)
    c: Coincident(g806,g807)
    c: Coincident(g859,g861)
    c: Coincident(g862,g864)
    c: Coincident(g809,g810)
    c: Coincident(g860,g862)
    c: Coincident(g780,g781)
    c: Coincident(g852,g853)
    c: Coincident(g856,g857)
    c: Coincident(g832,g833)
    c: Coincident(g798,g799)
    c: Coincident(g857,g859)
    c: Coincident(g24,g27)
    c: Coincident(g33,g34)
    c: Coincident(g808,g809)
    c: Coincident(g803,g804)
    c: Coincident(g853,g854)
    c: Coincident(g800,g801)
    c: Coincident(g26,g27)
    c: Coincident(g34,g35)
    c: Coincident(g832,g855)
    c: Coincident(g805,g806)
    c: Coincident(g799,g800)
    c: Coincident(g804,g805)
    c: Coincident(g779,g780)
    c: Coincident(g854,g855)
    c: Coincident(g801,g802)
    c: Coincident(g858,g860)
    c: Coincident(g856,g858)
    c: Coincident(g779,g802)
    c: Coincident(g28,g31)
    c: Coincident(g30,g31)
FEATURE [PartDesign::Pad] Pad007
  BaseFeature = -> Fillet011
  Direction = (0,0,-1)
  Length = 1.5
  Length2 = 10
  Profile = -> Sketch023
  ReferenceAxis = -> Sketch023 [N_Axis]
  Refine = true
  Suppressed = false
  Type = 0
  expr: Length = 1.5
FEATURE [PartDesign::Body] Body022  label="desc_upper_ring"
  AllowCompound = false
  Group = -> [Sketch021,Pad006,Sketch022,Pocket006,PolarPattern005,Fillet010,Fillet011,Sketch023,Pad007]
  Origin = -> Origin036
  Tip = -> Pad007
FEATURE [App::Link] desc_upper_ring
  LinkPlacement = pos=(4.7e-15,4.3e-15,41.6) rot=(-1,0,0;3.14159rad)
  LinkedObject = -> Body022
  Placement = pos=(4.7e-15,4.3e-15,41.6) rot=(-1,0,0;3.14159rad)
FEATURE [PartDesign::Fillet] Fillet012
  Base = -> Pocket004 [Face5,Face4]
  BaseFeature = -> Pocket004
  Radius = 0.25
  Refine = true
  SupportTransform = false
  Suppressed = false
  UseAllEdges = false
  expr: Radius = 0.25
FEATURE [PartDesign::Body] Body005  label="motor_gear001"
  AllowCompound = false
  Group = -> [InvoluteGear001,Sketch008,Pocket004,Fillet012]
  Origin = -> Origin010
  Placement = pos=(0,0,75) rot=(0,0,1;0rad)
  Tip = -> Fillet012
FEATURE [App::FeaturePython] GroundedJoint  # Assembly grounded joint (typed FeaturePython)
  ObjectToGround = -> Body006
FEATURE [App::FeaturePython] Joint  label="Revolute"  # Assembly joint (typed FeaturePython)
  Activated = true
  AngleMax = 0
  AngleMin = 0
  Detach1 = false
  Detach2 = false
  Distance = 0
  Distance2 = 0
  EnableAngleMax = false
  EnableAngleMin = false
  EnableLengthMax = false
  EnableLengthMin = false
  JointType = 1 (Revolute)
  LengthMax = 0
  LengthMin = 0
  Placement1 = pos=(2.47483e-06,9.04337e-05,56) rot=(0,0,1;0rad)
  Placement2 = pos=(34.5,0,1) rot=(0,0,1;0rad)
  Reference1 = -> Assembly [Body019.Face435,Body019.Face435]
  Reference2 = -> Assembly [Body006.Face93,Body006.Edge2]
  Suppressed = false
FEATURE [App::FeaturePython] Joint001  label="Revolute002"  # Assembly joint (typed FeaturePython)
  Activated = true
  AngleMax = 0
  AngleMin = 0
  Detach1 = false
  Detach2 = false
  Distance = 0
  Distance2 = 0
  EnableAngleMax = false
  EnableAngleMin = false
  EnableLengthMax = false
  EnableLengthMin = false
  JointType = 1 (Revolute)
  LengthMax = 0
  LengthMin = 0
  Reference1 = -> Assembly [outer_gear.,outer_gear.]
  Suppressed = false
FEATURE [App::FeaturePython] Joint002  label="Revolute004"  # Assembly joint (typed FeaturePython)
  Activated = true
  AngleMax = 0
  AngleMin = 0
  Detach1 = false
  Detach2 = false
  Distance = 0
  Distance2 = 0
  EnableAngleMax = false
  EnableAngleMin = false
  EnableLengthMax = false
  EnableLengthMin = false
  JointType = 1 (Revolute)
  LengthMax = 0
  LengthMin = 0
  Suppressed = false
FEATURE [App::FeaturePython] Joint003  label="Revolute005"  # Assembly joint (typed FeaturePython)
  Activated = true
  AngleMax = 0
  AngleMin = 0
  Detach1 = false
  Detach2 = false
  Distance = 0
  Distance2 = 0
  EnableAngleMax = false
  EnableAngleMin = false
  EnableLengthMax = false
  EnableLengthMin = false
  JointType = 1 (Revolute)
  LengthMax = 0
  LengthMin = 0
  Suppressed = false
FEATURE [App::FeaturePython] Joint004  label="Revolute006"  # Assembly joint (typed FeaturePython)
  Activated = true
  AngleMax = 0
  AngleMin = 0
  Detach1 = false
  Detach2 = false
  Distance = 0
  Distance2 = 0
  EnableAngleMax = false
  EnableAngleMin = false
  EnableLengthMax = false
  EnableLengthMin = false
  JointType = 1 (Revolute)
  LengthMax = 0
  LengthMin = 0
  Suppressed = false
FEATURE [Sketcher::SketchObject] Sketch024
  ArcFitTolerance = 1e-06
  AttachmentSupport = -> [Origin040]
  FullyConstrained = true
  MakeInternals = false
  MapMode = 5
  sketch-geometry (5):
    g0: ArcOfCircle CenterX=0 CenterY=0 CenterZ=0 NormalX=0 NormalY=0 NormalZ=1 AngleXU=0 Radius=100 StartAngle=4.71239 EndAngle=10.7992
    g1: ArcOfCircle CenterX=0 CenterY=0 CenterZ=0 NormalX=0 NormalY=0 NormalZ=1 AngleXU=0 Radius=41 StartAngle=4.51604 EndAngle=4.71239
    g2: Circle CenterX=0 CenterY=0 CenterZ=0 NormalX=0 NormalY=0 NormalZ=1 AngleXU=0 Radius=38
    g3: LineSegment StartX=-7.5e-15 StartY=-41 StartZ=0 EndX=-1.84e-14 EndY=-100 EndZ=0
    g4: LineSegment StartX=-19.509 StartY=-98.0785 StartZ=0 EndX=-7.99869 EndY=-40.2122 EndZ=0
  constraints (14):
    c: Angle(g0) = 6.08684
    c: Coincident(g0,g-1)
    c: PointOnObject(g0,g-2)
    c: Coincident(g1,g0)
    c: PointOnObject(g1,g-2)
    c: Diameter(g2) = 76
    c: Coincident(g2,g0)
    c: Radius(g0) = 100
    c: Distance(g1,g2) = 3
    c: Coincident(g3,g1)
    c: Coincident(g3,g0)
    c: Coincident(g4,g0)
    c: Coincident(g4,g1)
    c: PointOnObject(g0,g4)
FEATURE [PartDesign::Pad] Pad008
  Direction = (0,0,1)
  Length = 1.5
  Length2 = 10
  Profile = -> Sketch024
  ReferenceAxis = -> Sketch024 [N_Axis]
  Refine = true
  Suppressed = false
  Type = 0
  expr: Length = 1.5
FEATURE [Sketcher::SketchObject] Sketch025
  ArcFitTolerance = 1e-06
  ExternalGeometry = -> [Pad008]
  FullyConstrained = false
  MakeInternals = false
  MapMode = 5
  Placement = pos=(-1.84e-14,-100,0) rot=(0.57735,-0.57735,-0.57735;2.0944rad)
  sketch-geometry (10):
    g0: LineSegment StartX=0 StartY=0 StartZ=0 EndX=0.693802 EndY=-1.2017 EndZ=0
    g1: LineSegment StartX=1.21047 StartY=-1.5 StartZ=0 EndX=2.01139 EndY=-1.5 EndZ=0
    g2: LineSegment StartX=2.37172 StartY=-0.875891 StartZ=0 EndX=1.18232 EndY=1.18422 EndZ=0
    g3: LineSegment StartX=0.63537 StartY=1.5 StartZ=0 EndX=0 EndY=1.5 EndZ=0
    g4: ArcOfCircle CenterX=0.63537 CenterY=0.868442 CenterZ=0 NormalX=0 NormalY=0 NormalZ=1 AngleXU=0 Radius=0.631558 StartAngle=0.523599 EndAngle=1.5708
    g5: GeomPoint [constr] X=1 Y=1.5 Z=0
    g6: ArcOfCircle CenterX=2.01139 CenterY=-1.08393 CenterZ=0 NormalX=0 NormalY=0 NormalZ=1 AngleXU=0 Radius=0.416073 StartAngle=4.71239 EndAngle=6.80678
    g7: GeomPoint [constr] X=2.73205 Y=-1.5 Z=0
    g8: ArcOfCircle CenterX=1.21047 CenterY=-0.903401 CenterZ=0 NormalX=0 NormalY=0 NormalZ=1 AngleXU=0 Radius=0.596599 StartAngle=3.66519 EndAngle=4.71239
    g9: GeomPoint [constr] X=0.866025 Y=-1.5 Z=0
  constraints (20):
    c: Coincident(g-3,g0)
    c: Coincident(g3,g-3)
    c: Horizontal(g3)
    c: Parallel(g0,g2)
    c: Parallel(g1,g3)
    c: Angle(g-2,g0) = 0.523599
    c: Distance(g5,g1) = 3
    c: DistanceX(g3,g5) = 1
    c: PointOnObject(g5,g3)
    c: PointOnObject(g5,g2)
    c: Tangent(g3,g4) = -1.5708
    c: Tangent(g2,g4) = -1.5708
    c: PointOnObject(g7,g2)
    c: PointOnObject(g7,g1)
    c: Tangent(g2,g6) = -1.5708
    c: Tangent(g1,g6) = -1.5708
    c: PointOnObject(g9,g1)
    c: PointOnObject(g9,g0)
    c: Tangent(g1,g8) = -1.5708
    c: Tangent(g0,g8) = -1.5708
FEATURE [PartDesign::Revolution] Revolution007
  Angle = 360
  Angle2 = 348.75
  Axis = (0,0,1)
  Base = (0,0,0)
  BaseFeature = -> Pad008
  Profile = -> Sketch025
  ReferenceAxis = -> Pad008 [Edge3]
  Refine = true
  Reversed = true
  Suppressed = false
  Type = 4
FEATURE [Sketcher::SketchObject] Sketch026
  ArcFitTolerance = 1e-06
  AttachmentSupport = -> [Revolution007]
  ExternalGeometry = -> [Revolution007]
  FullyConstrained = true
  MakeInternals = false
  MapMode = 5
  Placement = pos=(0,0,0) rot=(1,0,0;3.14159rad)
  sketch-geometry (1):
    g0: Circle CenterX=0 CenterY=0 CenterZ=0 NormalX=0 NormalY=0 NormalZ=1 AngleXU=0 Radius=41
  constraints (2):
    c: Coincident(g0,g-3)
    c: PointOnObject(g-4,g0)
FEATURE [PartDesign::Pad] Pad009
  BaseFeature = -> Revolution007
  Direction = (0,0,-1)
  Length = 3
  Length2 = 10
  Profile = -> Sketch026
  ReferenceAxis = -> Sketch026 [N_Axis]
  Refine = true
  Suppressed = false
  Type = 0
  expr: Length = 3
FEATURE [PartDesign::Chamfer] Chamfer001
  Angle = 45
  Base = -> Pad009 [Edge34]
  BaseFeature = -> Pad009
  ChamferType = 0
  FlipDirection = false
  Refine = true
  Size = 2
  Size2 = 1
  SupportTransform = false
  Suppressed = false
  UseAllEdges = false
  expr: Size = 2
FEATURE [PartDesign::Fillet] Fillet013
  Base = -> Chamfer001 [Edge1,Edge2,Edge24,Edge19]
  BaseFeature = -> Chamfer001
  Radius = 0.5
  Refine = true
  SupportTransform = false
  Suppressed = false
  UseAllEdges = false
  expr: Radius = 0.5
FEATURE [PartDesign::Body] Body023  label="cover"
  AllowCompound = false
  Group = -> [Sketch024,Pad008,Sketch025,Revolution007,Sketch026,Pad009,Chamfer001,Fillet013]
  Origin = -> Origin040
  Placement = pos=(-3.2e-15,-3.5e-15,43) rot=(0,0,-1;6.08242rad)
  Tip = -> Fillet013
FEATURE [App::FeaturePython] Joint005  label="Revolute007"  # Assembly joint (typed FeaturePython)
  Activated = true
  AngleMax = 0
  AngleMin = 0
  Detach1 = false
  Detach2 = false
  Distance = 0
  Distance2 = 0
  EnableAngleMax = false
  EnableAngleMin = false
  EnableLengthMax = false
  EnableLengthMin = false
  JointType = 1 (Revolute)
  LengthMax = 0
  LengthMin = 0
  Suppressed = false
FEATURE [Assembly::JointGroup] Joints
  Group = -> [GroundedJoint,Joint,Joint001,Joint002,Joint003,Joint004,Joint005]
FEATURE [Assembly::AssemblyObject] Assembly
  Group = -> [Joints,Body006,Body019,motor_gear001,outer_gear,upper_cover_display,desc_upper_ring,GroundedJoint,Joint,Joint001,Joint002,Joint003,Joint004,Body023,Joint005]
  Origin = -> Origin038
  Type = Assembly
FEATURE [TechDraw::DrawSVGTemplate] Template
  Height = 210
  Orientation = 1
  Template = <path>
  Width = 297
FEATURE [TechDraw::DrawProjGroupItem] View
  CoarseView = false
  Direction = (0,-1,1)
  Focus = 100
  HardHidden = false
  IsoCount = 0
  IsoHidden = false
  IsoVisible = false
  LockPosition = false
  Perspective = false
  Rotation = 0
  RotationVector = (1,0,0)
  ScaleType = 0
  ScrubCount = 1
  SeamHidden = false
  SeamVisible = false
  SmoothHidden = false
  SmoothVisible = true
  Type = 0
  X = 148.5
  XDirection = (1,0,0)
  XSource = -> [Body006,Body019,motor_gear001]
  Y = 105
FEATURE [TechDraw::DrawPage] Page
  KeepUpdated = true
  NextBalloonIndex = 1
  ProjectionType = 0
  Template = -> Template
  Views = -> [View]
FEATURE [TechDraw::DrawSVGTemplate] Template001
  Height = 210
  Orientation = 1
  Template = <path>
  Width = 297
FEATURE [TechDraw::DrawProjGroupItem] View001
  CoarseView = false
  Direction = (0,-1,1)
  Focus = 100
  HardHidden = false
  IsoCount = 0
  IsoHidden = false
  IsoVisible = false
  LockPosition = false
  Perspective = false
  Rotation = 0
  RotationVector = (1,0,0)
  ScaleType = 0
  ScrubCount = 1
  SeamHidden = false
  SeamVisible = false
  SmoothHidden = false
  SmoothVisible = true
  Type = 0
  X = 148.77
  XDirection = (1,0,0)
  XSource = -> [upper_cover_display,outer_gear,desc_upper_ring]
  Y = 104.86
FEATURE [TechDraw::DrawSVGTemplate] Template002
  Height = 210
  Orientation = 1
  Template = <path>
  Width = 297
FEATURE [TechDraw::DrawProjGroupItem] View002
  CoarseView = false
  Direction = (0,-1,1)
  Focus = 100
  HardHidden = false
  IsoCount = 0
  IsoHidden = false
  IsoVisible = false
  LockPosition = false
  Perspective = false
  Rotation = 0
  RotationVector = (1,0,0)
  ScaleType = 0
  ScrubCount = 1
  SeamHidden = false
  SeamVisible = false
  SmoothHidden = false
  SmoothVisible = true
  Source = -> [Body023]
  Type = 0
  X = 148.5
  XDirection = (1,0,0)
  Y = 105
FEATURE [TechDraw::DrawPage] Page002
  KeepUpdated = true
  NextBalloonIndex = 1
  ProjectionType = 0
  Template = -> Template002
  Views = -> [View002]
FEATURE [TechDraw::DrawViewDimension] Dimension
  AngleOverride = false
  Arbitrary = false
  ArbitraryTolerances = false
  BoxCorners = (2) [(-99.3828,-75.2227,-1e-07),(99.3828,75.2227,1e-07)]
  EqualTolerance = true
  ExtensionAngle = 0
  FormatSpec = %.2w
  FormatSpecOverTolerance = %+.2w
  FormatSpecUnderTolerance = %+.2w
  Inverted = false
  LineAngle = 0
  LockPosition = false
  MeasureType = 1
  OverTolerance = 0
  References2D = -> [View001]
  Rotation = 0
  ScaleType = 0
  TheoreticalExact = false
  Type = 1
  UnderTolerance = 0
  X = 5.00916
  Y = 83.8089
FEATURE [TechDraw::DrawViewDimension] Dimension001
  AngleOverride = false
  Arbitrary = false
  ArbitraryTolerances = false
  BoxCorners = (2) [(-99.3828,-75.2227,-1e-07),(99.3828,75.2227,1e-07)]
  EqualTolerance = true
  ExtensionAngle = 0
  FormatSpec = %.2w
  FormatSpecOverTolerance = %+.2w
  FormatSpecUnderTolerance = %+.2w
  Inverted = false
  LineAngle = 0
  LockPosition = false
  MeasureType = 1
  OverTolerance = 0
  References2D = -> [View001]
  Rotation = 0
  ScaleType = 0
  TheoreticalExact = false
  Type = 1
  UnderTolerance = 0
  X = 75.1269
  Y = -62.2223
FEATURE [TechDraw::DrawPage] Page001
  KeepUpdated = true
  NextBalloonIndex = 2
  ProjectionType = 0
  Template = -> Template001
  Views = -> [View001,Dimension,Dimension001]
FEATURE [Sketcher::SketchObject] Sketch027
  ArcFitTolerance = 1e-06
  AttachmentSupport = -> [Fillet008]
  ExternalGeometry = -> [Fillet008]
  FullyConstrained = true
  MakeInternals = false
  MapMode = 5
  Placement = pos=(7e-16,7e-16,6) rot=(0,0,1;0rad)
  expr: Constraints[7] = 1
  sketch-geometry (4):
    g0: Circle CenterX=0 CenterY=0 CenterZ=0 NormalX=0 NormalY=0 NormalZ=1 AngleXU=0 Radius=51
    g1: Circle CenterX=0 CenterY=0 CenterZ=0 NormalX=0 NormalY=0 NormalZ=1 AngleXU=0 Radius=76.3276
    g2: Circle CenterX=0 CenterY=0 CenterZ=0 NormalX=0 NormalY=0 NormalZ=1 AngleXU=0 Radius=73.8276
    g3: Circle CenterX=0 CenterY=0 CenterZ=0 NormalX=0 NormalY=0 NormalZ=1 AngleXU=0 Radius=68.8276
  constraints (11):
    c: PointOnObject(g0,g-1)
    c: PointOnObject(g0,g-2)
    c: Distance(g0,g-3) = 5
    c: PointOnObject(g1,g-1)
    c: PointOnObject(g2,g-1)
    c: PointOnObject(g2,g-2)
    c: PointOnObject(g1,g-2)
    c: Distance(g1,g-4) = 1
    c: Distance(g1,g2) = 2.5
    c: Coincident(g3,g0)
    c: Distance(g2,g3) = 5
FEATURE [PartDesign::Body] Body003
  AllowCompound = false
  Group = -> [Sketch003,Pad,Sketch004,Pad001,Sketch005,Pocket001,Sketch006,Pocket002,Sketch007,Pocket003,Sketch009,Revolution,Fillet,Sketch019,Sketch020,Revolution005,Revolution006,PolarPattern004,Fillet005,Fillet006,Fillet007,Fillet008,Sketch027]
  Origin = -> Origin006
  Tip = -> Fillet008
FEATURE [Measure::MeasurePython] Center_of_mass  label="Center_of_mass: "  # WARN: FeaturePython — macro-defined, semantics opaque (R4)
  Element = -> Body003 [Pad001.Sketch004.]
  Placement = pos=(2.274e-13,3e-15,6) rot=(0,0,1;0rad)
  Result = (2.274e-13,3e-15,6)
note: 3 file-system paths scrubbed to <path> (originals preserved in the JSON sidecar)
